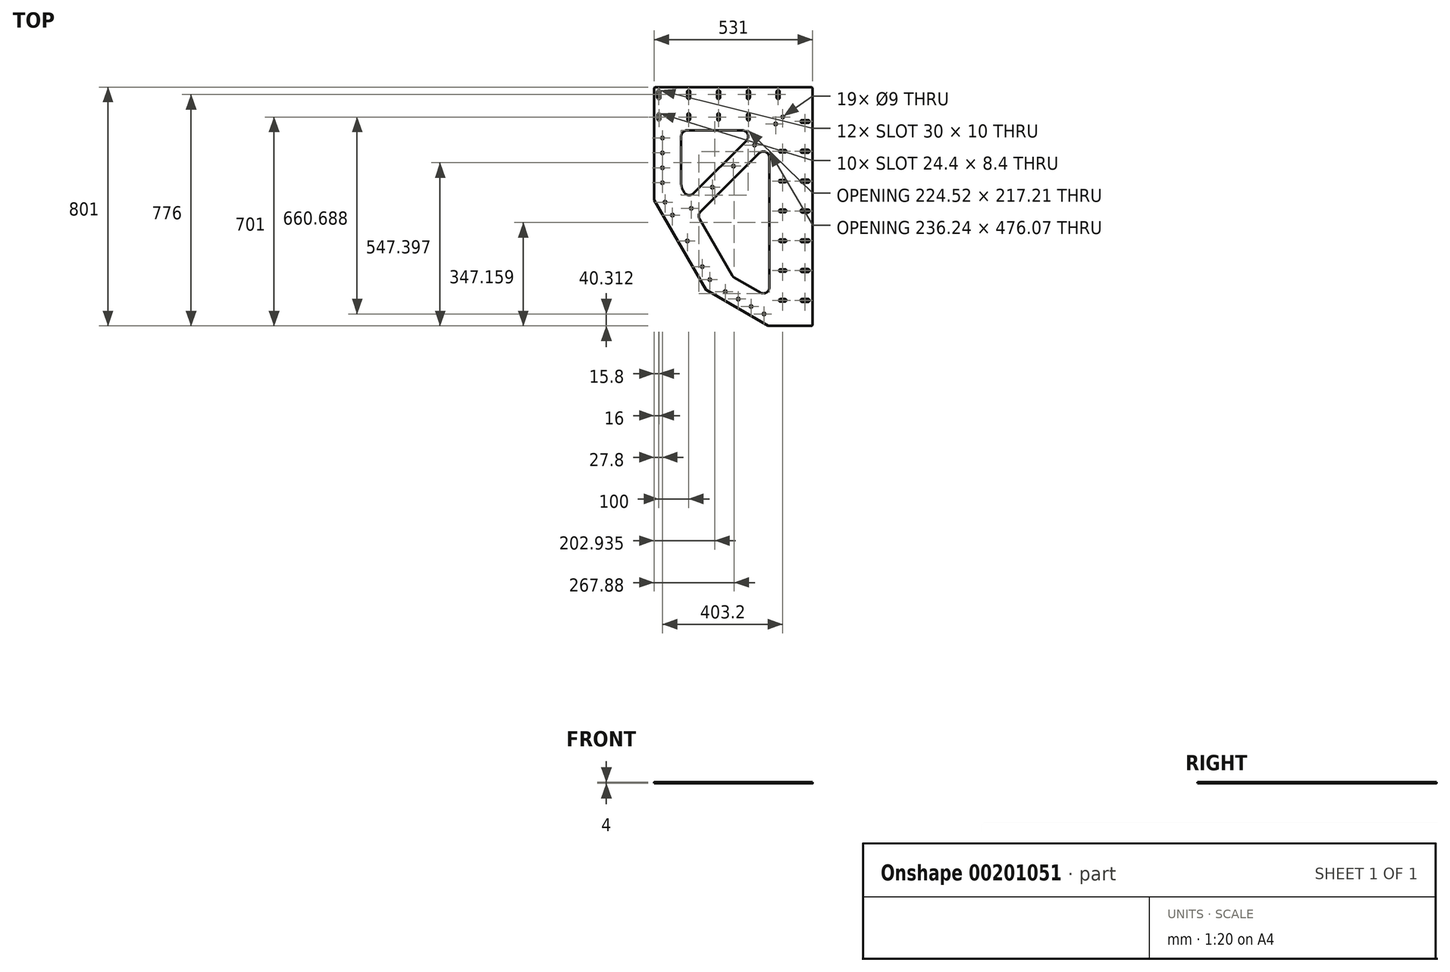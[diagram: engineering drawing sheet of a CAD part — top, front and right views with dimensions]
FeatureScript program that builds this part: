
annotation { "Feature Type Name" : "Feature", "Feature Type Description" : "" }
export const myFeature = defineFeature(function(context is Context, id is Id, definition is map)
    precondition{}
    {
        {
            var Q0;
            Q0=qCreatedBy(makeId("Top.planeOp"),FACE);
            var sketch = newSketch(context, id + "F0", { "sketchPlane" : qUnion([Q0])});
            skLineSegment(sketch, "E0.bottom", {"start": v(750, -750) * mm, "end": v(-750, -750) * mm});
            skLineSegment(sketch, "E0.top", {"start": v(750, 750) * mm, "end": v(-750, 750) * mm});
            skLineSegment(sketch, "E0.left", {"start": v(750, -750) * mm, "end": v(750, 750) * mm});
            skLineSegment(sketch, "E0.right", {"start": v(-750, -750) * mm, "end": v(-750, 750) * mm});
            skPoint(sketch, "E0.middle", {"position": v(0, 0) * mm});
            skSolve(sketch);
        }
        {
            var Q0;
            Q0=qSketchRegion(id+"F0",true);
            extrude(context, id + "F1", {"entities" : qUnion([Q0]), "depth" : 4 * mm});
        }
        {
            var Q0;
            Q0=makeQuery(id+"F1.opExtrude","CAP_FACE",FACE,{"disambiguationData":[OSD([sQuery(id+"F0.wireOp",EDGE,"E0.bottom"),sQuery(id+"F0.wireOp",EDGE,"E0.top"),sQuery(id+"F0.wireOp",EDGE,"E0.left"),sQuery(id+"F0.wireOp",EDGE,"E0.right")])],"isStart":false});
            var sketch = newSketch(context, id + "F2", { "sketchPlane" : qUnion([Q0])});
            skLineSegment(sketch, "E1", {"start": v(0, -750) * mm, "end": v(0, 750) * mm, "construction": true});
            skCircle(sketch, "E2", {"center": v(0, 71) * mm, "radius": 559 * mm, "construction": true});
            skCircle(sketch, "E3", {"center": v(0, 630) * mm, "radius": 7.5 * mm});
            skLineSegment(sketch, "E4", {"start": v(0, 71) * mm, "end": v(-275.24, -87.91) * mm, "construction": true});
            skLineSegment(sketch, "E5", {"start": v(0, 71) * mm, "end": v(329.13, -119.03) * mm, "construction": true});
            skCircle(sketch, "E6.MirrorC", {"center": v(-484.1, -208.5) * mm, "radius": 7.5 * mm});
            skCircle(sketch, "E7.MirrorC", {"center": v(484.1, -208.5) * mm, "radius": 7.5 * mm});
            skCircle(sketch, "E8", {"center": v(0, 71) * mm, "radius": 362 * mm, "construction": true});
            skCircle(sketch, "E9", {"center": v(0, 71) * mm, "radius": 409.5 * mm, "construction": true});
            skCircle(sketch, "E10", {"center": v(-92, 470.03) * mm, "radius": 7.5 * mm});
            skCircle(sketch, "E11.MirrorC", {"center": v(92, 470.03) * mm, "radius": 7.5 * mm});
            skCircle(sketch, "E12", {"center": v(-127, 410) * mm, "radius": 7.5 * mm});
            skCircle(sketch, "E13.MirrorC", {"center": v(127, 410) * mm, "radius": 7.5 * mm});
            skCircle(sketch, "E14.MirrorC", {"center": v(-230.07, -208.48) * mm, "radius": 7.5 * mm});
            skCircle(sketch, "E15.MirrorC", {"center": v(-357.07, 11.49) * mm, "radius": 7.5 * mm});
            skCircle(sketch, "E16.MirrorC", {"center": v(-299.57, -208.2) * mm, "radius": 7.5 * mm});
            skCircle(sketch, "E17.MirrorC", {"center": v(-391.57, -48.84) * mm, "radius": 7.5 * mm});
            skCircle(sketch, "E18.MirrorC", {"center": v(391.57, -48.84) * mm, "radius": 7.5 * mm});
            skCircle(sketch, "E19.MirrorC", {"center": v(299.57, -208.2) * mm, "radius": 7.5 * mm});
            skCircle(sketch, "E20.MirrorC", {"center": v(230.07, -208.48) * mm, "radius": 7.5 * mm});
            skCircle(sketch, "E21.MirrorC", {"center": v(357.07, 11.49) * mm, "radius": 7.5 * mm});
            skPoint(sketch, "E22.middle", {"position": v(0, 435.08) * mm});
            skCircle(sketch, "E23", {"center": v(0, 430) * mm, "radius": 7.5 * mm});
            skCircle(sketch, "E24.MirrorC", {"center": v(310.9, -108.5) * mm, "radius": 7.5 * mm});
            skCircle(sketch, "E25.MirrorC", {"center": v(-310.9, -108.5) * mm, "radius": 7.5 * mm});
            skSolve(sketch);
        }
        {
            var Q0;
            Q0=qSketchRegion(id+"F2",true);
            extrude(context, id + "F3", {"entities" : qUnion([Q0]), "operationType" : NewBodyOperationType.REMOVE, "endBound" : BoundingType.THROUGH_ALL, "oppositeDirection" : true, "depth" : 25 * mm});
        }
        {
            var Q0;
            Q0=makeQuery(id+"F1.opExtrude","CAP_FACE",FACE,{"disambiguationData":[OSD([sQuery(id+"F0.wireOp",EDGE,"E0.bottom"),sQuery(id+"F0.wireOp",EDGE,"E0.top"),sQuery(id+"F0.wireOp",EDGE,"E0.left"),sQuery(id+"F0.wireOp",EDGE,"E0.right")])],"isStart":false});
            var sketch = newSketch(context, id + "F4", { "sketchPlane" : qUnion([Q0])});
            skLineSegment(sketch, "E26", {"start": v(0, 750) * mm, "end": v(0, -750) * mm, "construction": true});
            skLineSegment(sketch, "E27", {"start": v(-627.57, 670) * mm, "end": v(-374.68, 670) * mm});
            skLineSegment(sketch, "E28", {"start": v(-397.7, 440.12) * mm, "end": v(-627.57, 670) * mm});
            skLineSegment(sketch, "E29.MirrorCS", {"start": v(627.57, 670) * mm, "end": v(374.68, 670) * mm});
            skLineSegment(sketch, "E30.MirrorCS", {"start": v(397.7, 440.12) * mm, "end": v(627.57, 670) * mm});
            skLineSegment(sketch, "E31", {"start": v(-257.5, 299.93) * mm, "end": v(257.5, 299.93) * mm, "construction": true});
            skLineSegment(sketch, "E32", {"start": v(257.5, 299.93) * mm, "end": v(0, 42.43) * mm});
            skLineSegment(sketch, "E33.MirrorCS", {"start": v(-257.5, 299.93) * mm, "end": v(0, 42.43) * mm});
            skLineSegment(sketch, "E34", {"start": v(-399.35, 0) * mm, "end": v(437.87, 0) * mm, "construction": true});
            skLineSegment(sketch, "E35.MirrorCS", {"start": v(-257.5, -299.93) * mm, "end": v(0, -42.43) * mm});
            skLineSegment(sketch, "E36.MirrorCS", {"start": v(-257.5, -299.93) * mm, "end": v(257.5, -299.93) * mm, "construction": true});
            skLineSegment(sketch, "E37.MirrorCS", {"start": v(257.5, -299.93) * mm, "end": v(0, -42.43) * mm});
            skLineSegment(sketch, "E38", {"start": v(-215.67, -173.24) * mm, "end": v(-42.43, 0) * mm});
            skLineSegment(sketch, "E39.MirrorCS", {"start": v(-215.67, 173.24) * mm, "end": v(-42.43, 0) * mm});
            skLineSegment(sketch, "E40.MirrorCS", {"start": v(215.67, 173.24) * mm, "end": v(42.43, 0) * mm});
            skLineSegment(sketch, "E41.MirrorCS", {"start": v(215.67, -173.24) * mm, "end": v(42.43, 0) * mm});
            skLineSegment(sketch, "E42", {"start": v(750, 750) * mm, "end": v(-750, -750) * mm, "construction": true});
            skLineSegment(sketch, "E43", {"start": v(-750, 750) * mm, "end": v(750, -750) * mm, "construction": true});
            skLineSegment(sketch, "E44", {"start": v(-750, -707.57) * mm, "end": v(707.57, 750) * mm, "construction": true});
            skLineSegment(sketch, "E45", {"start": v(750, 707.57) * mm, "end": v(-707.57, -750) * mm, "construction": true});
            skLineSegment(sketch, "E46", {"start": v(-215.67, 173.24) * mm, "end": v(-315.69, 0) * mm, "construction": true});
            skLineSegment(sketch, "E47", {"start": v(-315.69, 0) * mm, "end": v(-215.67, -173.24) * mm});
            skLineSegment(sketch, "E48.MirrorCS", {"start": v(315.69, 0) * mm, "end": v(215.67, -173.24) * mm});
            skLineSegment(sketch, "E49.MirrorCS", {"start": v(215.67, 173.24) * mm, "end": v(315.69, 0) * mm, "construction": true});
            skLineSegment(sketch, "E50", {"start": v(670, 627.57) * mm, "end": v(428.76, 386.33) * mm});
            skLineSegment(sketch, "E51", {"start": v(670, 108.48) * mm, "end": v(670, 627.57) * mm});
            skLineSegment(sketch, "E52", {"start": v(-184.6, -227.04) * mm, "end": v(-257.5, -299.93) * mm});
            skLineSegment(sketch, "E53", {"start": v(-184.6, -227.04) * mm, "end": v(184.6, -227.04) * mm, "construction": true});
            skLineSegment(sketch, "E54", {"start": v(257.5, -299.93) * mm, "end": v(184.6, -227.04) * mm});
            skLineSegment(sketch, "E55", {"start": v(-670, -227.57) * mm, "end": v(-670, -627.57) * mm});
            skLineSegment(sketch, "E56", {"start": v(-670, -627.57) * mm, "end": v(-523.59, -481.16) * mm});
            skLineSegment(sketch, "E57", {"start": v(-523.59, -481.16) * mm, "end": v(-670, -227.57) * mm});
            skLineSegment(sketch, "E58.MirrorCS", {"start": v(523.59, -481.16) * mm, "end": v(670, -227.57) * mm});
            skLineSegment(sketch, "E59.MirrorCS", {"start": v(670, -627.57) * mm, "end": v(523.59, -481.16) * mm});
            skLineSegment(sketch, "E60.MirrorCS", {"start": v(670, -227.57) * mm, "end": v(670, -627.57) * mm});
            skLineSegment(sketch, "E61", {"start": v(0, -450) * mm, "end": v(-117.15, -450) * mm});
            skLineSegment(sketch, "E62", {"start": v(-117.15, -450) * mm, "end": v(-325, -570) * mm});
            skLineSegment(sketch, "E63", {"start": v(-325, -570) * mm, "end": v(0, -570) * mm, "construction": true});
            skLineSegment(sketch, "E64.MirrorCS", {"start": v(0, -450) * mm, "end": v(117.15, -450) * mm});
            skLineSegment(sketch, "E65.MirrorCS", {"start": v(325, -570) * mm, "end": v(0, -570) * mm, "construction": true});
            skLineSegment(sketch, "E66.MirrorCS", {"start": v(117.15, -450) * mm, "end": v(325, -570) * mm});
            skLineSegment(sketch, "E67.MirrorCS", {"start": v(-670, 108.48) * mm, "end": v(-670, 627.57) * mm});
            skLineSegment(sketch, "E68.MirrorCS", {"start": v(-670, 627.57) * mm, "end": v(-428.76, 386.33) * mm});
            skLineSegment(sketch, "E69", {"start": v(428.76, 386.33) * mm, "end": v(548.76, 178.48) * mm});
            skLineSegment(sketch, "E70", {"start": v(548.76, 178.48) * mm, "end": v(670, 108.48) * mm});
            skLineSegment(sketch, "E71.MirrorCS", {"start": v(-428.76, 386.33) * mm, "end": v(-548.76, 178.48) * mm});
            skLineSegment(sketch, "E72.MirrorCS", {"start": v(-548.76, 178.48) * mm, "end": v(-670, 108.48) * mm});
            skLineSegment(sketch, "E73", {"start": v(-184.6, -227.04) * mm, "end": v(-152.63, -282.43) * mm});
            skLineSegment(sketch, "E74", {"start": v(-152.63, -282.43) * mm, "end": v(0, -282.43) * mm});
            skLineSegment(sketch, "E75.MirrorCS", {"start": v(152.63, -282.43) * mm, "end": v(0, -282.43) * mm});
            skLineSegment(sketch, "E76.MirrorCS", {"start": v(184.6, -227.04) * mm, "end": v(152.63, -282.43) * mm});
            skLineSegment(sketch, "E77", {"start": v(-408.03, 159.94) * mm, "end": v(-88.62, -393.3) * mm, "construction": true});
            skLineSegment(sketch, "E78", {"start": v(-215.67, 173.24) * mm, "end": v(-288.56, 246.13) * mm});
            skLineSegment(sketch, "E79", {"start": v(-288.56, 246.13) * mm, "end": v(-373.18, 99.57) * mm});
            skLineSegment(sketch, "E80", {"start": v(-315.69, 0) * mm, "end": v(-373.18, 99.57) * mm});
            skLineSegment(sketch, "E81.MirrorCS", {"start": v(288.56, 246.13) * mm, "end": v(373.18, 99.57) * mm});
            skLineSegment(sketch, "E82.MirrorCS", {"start": v(315.69, 0) * mm, "end": v(373.18, 99.57) * mm});
            skLineSegment(sketch, "E83.MirrorCS", {"start": v(215.67, 173.24) * mm, "end": v(288.56, 246.13) * mm});
            skLineSegment(sketch, "E84", {"start": v(-257.5, 299.93) * mm, "end": v(-462.8, -55.67) * mm, "construction": true});
            skLineSegment(sketch, "E85", {"start": v(-257.5, 299.93) * mm, "end": v(-211.31, 379.93) * mm});
            skLineSegment(sketch, "E86", {"start": v(-211.31, 379.93) * mm, "end": v(0, 379.93) * mm});
            skLineSegment(sketch, "E87.MirrorCS", {"start": v(211.31, 379.93) * mm, "end": v(0, 379.93) * mm});
            skLineSegment(sketch, "E88.MirrorCS", {"start": v(257.5, 299.93) * mm, "end": v(211.31, 379.93) * mm});
            skLineSegment(sketch, "E89", {"start": v(-325, -570) * mm, "end": v(-267.26, -670) * mm});
            skLineSegment(sketch, "E90", {"start": v(-267.26, -670) * mm, "end": v(0, -670) * mm});
            skLineSegment(sketch, "E91.MirrorCS", {"start": v(267.26, -670) * mm, "end": v(0, -670) * mm});
            skLineSegment(sketch, "E92.MirrorCS", {"start": v(325, -570) * mm, "end": v(267.26, -670) * mm});
            skLineSegment(sketch, "E93", {"start": v(428.76, 386.33) * mm, "end": v(397.7, 440.12) * mm, "construction": true});
            skLineSegment(sketch, "E94", {"start": v(397.7, 440.12) * mm, "end": v(374.68, 480) * mm});
            skLineSegment(sketch, "E95", {"start": v(374.68, 480) * mm, "end": v(374.68, 670) * mm});
            skLineSegment(sketch, "E96.MirrorCS", {"start": v(-374.68, 480) * mm, "end": v(-374.68, 670) * mm});
            skLineSegment(sketch, "E97.MirrorCS", {"start": v(-397.7, 440.12) * mm, "end": v(-374.68, 480) * mm});
            skSolve(sketch);
        }
        {
            var Q0;
            Q0=qSketchRegion(id+"F4",true);
            extrude(context, id + "F5", {"entities" : qUnion([Q0]), "operationType" : NewBodyOperationType.REMOVE, "endBound" : BoundingType.THROUGH_ALL, "oppositeDirection" : true, "depth" : 25 * mm});
        }
        {
            var Q0;
            Q0=makeQuery(id+"F1.opExtrude","CAP_FACE",FACE,{"disambiguationData":[OSD([sQuery(id+"F0.wireOp",EDGE,"E0.bottom"),sQuery(id+"F0.wireOp",EDGE,"E0.top"),sQuery(id+"F0.wireOp",EDGE,"E0.left"),sQuery(id+"F0.wireOp",EDGE,"E0.right")])],"isStart":false});
            var sketch = newSketch(context, id + "F6", { "sketchPlane" : qUnion([Q0])});
            skLineSegment(sketch, "E98", {"start": v(0, 750) * mm, "end": v(0, -750) * mm, "construction": true});
            skLineSegment(sketch, "E99.left", {"start": v(-595.8, 707) * mm, "end": v(-595.8, 723) * mm});
            skLineSegment(sketch, "E99.right", {"start": v(-604.2, 707) * mm, "end": v(-604.2, 723) * mm});
            skPoint(sketch, "E99.middle", {"position": v(-600, 715) * mm});
            skArc(sketch, "E100", {"start": v(-595.8, 723) * mm, "mid": v(-600, 727.2) * mm, "end": v(-604.2, 723) * mm});
            skArc(sketch, "E101", {"start": v(-604.2, 707) * mm, "mid": v(-600, 702.8) * mm, "end": v(-595.8, 707) * mm});
            skLineSegment(sketch, "E102", {"start": v(-604.2, 723) * mm, "end": v(-595.8, 723) * mm, "construction": true});
            skArc(sketch, "E103.1.0.0", {"start": v(-504.2, 707) * mm, "mid": v(-500, 702.8) * mm, "end": v(-495.8, 707) * mm});
            skLineSegment(sketch, "E103.1.0.1", {"start": v(-495.8, 707) * mm, "end": v(-495.8, 723) * mm});
            skArc(sketch, "E103.1.0.2", {"start": v(-495.8, 723) * mm, "mid": v(-500, 727.2) * mm, "end": v(-504.2, 723) * mm});
            skLineSegment(sketch, "E103.1.0.3", {"start": v(-504.2, 707) * mm, "end": v(-504.2, 723) * mm});
            skArc(sketch, "E103.2.0.0", {"start": v(-404.2, 707) * mm, "mid": v(-400, 702.8) * mm, "end": v(-395.8, 707) * mm});
            skLineSegment(sketch, "E103.2.0.1", {"start": v(-395.8, 707) * mm, "end": v(-395.8, 723) * mm});
            skArc(sketch, "E103.2.0.2", {"start": v(-395.8, 723) * mm, "mid": v(-400, 727.2) * mm, "end": v(-404.2, 723) * mm});
            skLineSegment(sketch, "E103.2.0.3", {"start": v(-404.2, 707) * mm, "end": v(-404.2, 723) * mm});
            skArc(sketch, "E103.3.0.0", {"start": v(-304.2, 707) * mm, "mid": v(-300, 702.8) * mm, "end": v(-295.8, 707) * mm});
            skLineSegment(sketch, "E103.3.0.1", {"start": v(-295.8, 707) * mm, "end": v(-295.8, 723) * mm});
            skArc(sketch, "E103.3.0.2", {"start": v(-295.8, 723) * mm, "mid": v(-300, 727.2) * mm, "end": v(-304.2, 723) * mm});
            skLineSegment(sketch, "E103.3.0.3", {"start": v(-304.2, 707) * mm, "end": v(-304.2, 723) * mm});
            skArc(sketch, "E103.4.0.0", {"start": v(-204.2, 707) * mm, "mid": v(-200, 702.8) * mm, "end": v(-195.8, 707) * mm});
            skLineSegment(sketch, "E103.4.0.1", {"start": v(-195.8, 707) * mm, "end": v(-195.8, 723) * mm});
            skArc(sketch, "E103.4.0.2", {"start": v(-195.8, 723) * mm, "mid": v(-200, 727.2) * mm, "end": v(-204.2, 723) * mm});
            skLineSegment(sketch, "E103.4.0.3", {"start": v(-204.2, 707) * mm, "end": v(-204.2, 723) * mm});
            skArc(sketch, "E103.5.0.0", {"start": v(-104.2, 707) * mm, "mid": v(-100, 702.8) * mm, "end": v(-95.8, 707) * mm});
            skLineSegment(sketch, "E103.5.0.1", {"start": v(-95.8, 707) * mm, "end": v(-95.8, 723) * mm});
            skArc(sketch, "E103.5.0.2", {"start": v(-95.8, 723) * mm, "mid": v(-100, 727.2) * mm, "end": v(-104.2, 723) * mm});
            skLineSegment(sketch, "E103.5.0.3", {"start": v(-104.2, 707) * mm, "end": v(-104.2, 723) * mm});
            skArc(sketch, "E103.6.0.0", {"start": v(-4.2, 707) * mm, "mid": v(0, 702.8) * mm, "end": v(4.2, 707) * mm});
            skLineSegment(sketch, "E103.6.0.1", {"start": v(4.2, 707) * mm, "end": v(4.2, 723) * mm});
            skArc(sketch, "E103.6.0.2", {"start": v(4.2, 723) * mm, "mid": v(0, 727.2) * mm, "end": v(-4.2, 723) * mm});
            skLineSegment(sketch, "E103.6.0.3", {"start": v(-4.2, 707) * mm, "end": v(-4.2, 723) * mm});
            skArc(sketch, "E103.7.0.0", {"start": v(95.8, 707) * mm, "mid": v(100, 702.8) * mm, "end": v(104.2, 707) * mm});
            skLineSegment(sketch, "E103.7.0.1", {"start": v(104.2, 707) * mm, "end": v(104.2, 723) * mm});
            skArc(sketch, "E103.7.0.2", {"start": v(104.2, 723) * mm, "mid": v(100, 727.2) * mm, "end": v(95.8, 723) * mm});
            skLineSegment(sketch, "E103.7.0.3", {"start": v(95.8, 707) * mm, "end": v(95.8, 723) * mm});
            skArc(sketch, "E103.8.0.0", {"start": v(195.8, 707) * mm, "mid": v(200, 702.8) * mm, "end": v(204.2, 707) * mm});
            skLineSegment(sketch, "E103.8.0.1", {"start": v(204.2, 707) * mm, "end": v(204.2, 723) * mm});
            skArc(sketch, "E103.8.0.2", {"start": v(204.2, 723) * mm, "mid": v(200, 727.2) * mm, "end": v(195.8, 723) * mm});
            skLineSegment(sketch, "E103.8.0.3", {"start": v(195.8, 707) * mm, "end": v(195.8, 723) * mm});
            skArc(sketch, "E103.9.0.0", {"start": v(295.8, 707) * mm, "mid": v(300, 702.8) * mm, "end": v(304.2, 707) * mm});
            skLineSegment(sketch, "E103.9.0.1", {"start": v(304.2, 707) * mm, "end": v(304.2, 723) * mm});
            skArc(sketch, "E103.9.0.2", {"start": v(304.2, 723) * mm, "mid": v(300, 727.2) * mm, "end": v(295.8, 723) * mm});
            skLineSegment(sketch, "E103.9.0.3", {"start": v(295.8, 707) * mm, "end": v(295.8, 723) * mm});
            skArc(sketch, "E103.10.0.0", {"start": v(395.8, 707) * mm, "mid": v(400, 702.8) * mm, "end": v(404.2, 707) * mm});
            skLineSegment(sketch, "E103.10.0.1", {"start": v(404.2, 707) * mm, "end": v(404.2, 723) * mm});
            skArc(sketch, "E103.10.0.2", {"start": v(404.2, 723) * mm, "mid": v(400, 727.2) * mm, "end": v(395.8, 723) * mm});
            skLineSegment(sketch, "E103.10.0.3", {"start": v(395.8, 707) * mm, "end": v(395.8, 723) * mm});
            skArc(sketch, "E103.11.0.0", {"start": v(495.8, 707) * mm, "mid": v(500, 702.8) * mm, "end": v(504.2, 707) * mm});
            skLineSegment(sketch, "E103.11.0.1", {"start": v(504.2, 707) * mm, "end": v(504.2, 723) * mm});
            skArc(sketch, "E103.11.0.2", {"start": v(504.2, 723) * mm, "mid": v(500, 727.2) * mm, "end": v(495.8, 723) * mm});
            skLineSegment(sketch, "E103.11.0.3", {"start": v(495.8, 707) * mm, "end": v(495.8, 723) * mm});
            skArc(sketch, "E103.12.0.0", {"start": v(595.8, 707) * mm, "mid": v(600, 702.8) * mm, "end": v(604.2, 707) * mm});
            skLineSegment(sketch, "E103.12.0.1", {"start": v(604.2, 707) * mm, "end": v(604.2, 723) * mm});
            skArc(sketch, "E103.12.0.2", {"start": v(604.2, 723) * mm, "mid": v(600, 727.2) * mm, "end": v(595.8, 723) * mm});
            skLineSegment(sketch, "E103.12.0.3", {"start": v(595.8, 707) * mm, "end": v(595.8, 723) * mm});
            skLineSegment(sketch, "E103.direction1", {"start": v(-604.2, 707) * mm, "end": v(-504.2, 707) * mm, "construction": true});
            skLineSegment(sketch, "E104", {"start": v(-750, 723) * mm, "end": v(750, 723) * mm, "construction": true});
            skLineSegment(sketch, "E105", {"start": v(-750, 0) * mm, "end": v(750, 0) * mm, "construction": true});
            skArc(sketch, "E106.MirrorCS", {"start": v(-295.8, -723) * mm, "mid": v(-300, -727.2) * mm, "end": v(-304.2, -723) * mm});
            skArc(sketch, "E107.MirrorCS", {"start": v(-495.8, -723) * mm, "mid": v(-500, -727.2) * mm, "end": v(-504.2, -723) * mm});
            skLineSegment(sketch, "E108.MirrorCS", {"start": v(304.2, -707) * mm, "end": v(304.2, -723) * mm});
            skLineSegment(sketch, "E109.MirrorCS", {"start": v(-495.8, -707) * mm, "end": v(-495.8, -723) * mm});
            skArc(sketch, "E110.MirrorCS", {"start": v(-504.2, -707) * mm, "mid": v(-500, -702.8) * mm, "end": v(-495.8, -707) * mm});
            skLineSegment(sketch, "E111.MirrorCS", {"start": v(-604.2, -723) * mm, "end": v(-595.8, -723) * mm, "construction": true});
            skArc(sketch, "E112.MirrorCS", {"start": v(-604.2, -707) * mm, "mid": v(-600, -702.8) * mm, "end": v(-595.8, -707) * mm});
            skArc(sketch, "E113.MirrorCS", {"start": v(-595.8, -723) * mm, "mid": v(-600, -727.2) * mm, "end": v(-604.2, -723) * mm});
            skLineSegment(sketch, "E114.MirrorCS", {"start": v(-604.2, -707) * mm, "end": v(-604.2, -723) * mm});
            skLineSegment(sketch, "E115.MirrorCS", {"start": v(-295.8, -707) * mm, "end": v(-295.8, -723) * mm});
            skLineSegment(sketch, "E116.MirrorCS", {"start": v(-595.8, -707) * mm, "end": v(-595.8, -723) * mm});
            skArc(sketch, "E117.MirrorCS", {"start": v(-304.2, -707) * mm, "mid": v(-300, -702.8) * mm, "end": v(-295.8, -707) * mm});
            skLineSegment(sketch, "E118.MirrorCS", {"start": v(-304.2, -707) * mm, "end": v(-304.2, -723) * mm});
            skArc(sketch, "E119.MirrorCS", {"start": v(295.8, -707) * mm, "mid": v(300, -702.8) * mm, "end": v(304.2, -707) * mm});
            skArc(sketch, "E120.MirrorCS", {"start": v(304.2, -723) * mm, "mid": v(300, -727.2) * mm, "end": v(295.8, -723) * mm});
            skLineSegment(sketch, "E121.MirrorCS", {"start": v(295.8, -707) * mm, "end": v(295.8, -723) * mm});
            skLineSegment(sketch, "E122.MirrorCS", {"start": v(-504.2, -707) * mm, "end": v(-504.2, -723) * mm});
            skArc(sketch, "E123.MirrorCS", {"start": v(-4.2, -707) * mm, "mid": v(0, -702.8) * mm, "end": v(4.2, -707) * mm});
            skArc(sketch, "E124.MirrorCS", {"start": v(104.2, -723) * mm, "mid": v(100, -727.2) * mm, "end": v(95.8, -723) * mm});
            skLineSegment(sketch, "E125.MirrorCS", {"start": v(-4.2, -707) * mm, "end": v(-4.2, -723) * mm});
            skArc(sketch, "E126.MirrorCS", {"start": v(4.2, -723) * mm, "mid": v(0, -727.2) * mm, "end": v(-4.2, -723) * mm});
            skLineSegment(sketch, "E127.MirrorCS", {"start": v(4.2, -707) * mm, "end": v(4.2, -723) * mm});
            skArc(sketch, "E128.MirrorCS", {"start": v(-195.8, -723) * mm, "mid": v(-200, -727.2) * mm, "end": v(-204.2, -723) * mm});
            skLineSegment(sketch, "E129.MirrorCS", {"start": v(395.8, -707) * mm, "end": v(395.8, -723) * mm});
            skArc(sketch, "E130.MirrorCS", {"start": v(504.2, -723) * mm, "mid": v(500, -727.2) * mm, "end": v(495.8, -723) * mm});
            skLineSegment(sketch, "E131.MirrorCS", {"start": v(-395.8, -707) * mm, "end": v(-395.8, -723) * mm});
            skArc(sketch, "E132.MirrorCS", {"start": v(395.8, -707) * mm, "mid": v(400, -702.8) * mm, "end": v(404.2, -707) * mm});
            skArc(sketch, "E133.MirrorCS", {"start": v(604.2, -723) * mm, "mid": v(600, -727.2) * mm, "end": v(595.8, -723) * mm});
            skLineSegment(sketch, "E134.MirrorCS", {"start": v(204.2, -707) * mm, "end": v(204.2, -723) * mm});
            skLineSegment(sketch, "E135.MirrorCS", {"start": v(-195.8, -707) * mm, "end": v(-195.8, -723) * mm});
            skArc(sketch, "E136.MirrorCS", {"start": v(-404.2, -707) * mm, "mid": v(-400, -702.8) * mm, "end": v(-395.8, -707) * mm});
            skLineSegment(sketch, "E137.MirrorCS", {"start": v(-95.8, -707) * mm, "end": v(-95.8, -723) * mm});
            skLineSegment(sketch, "E138.MirrorCS", {"start": v(495.8, -707) * mm, "end": v(495.8, -723) * mm});
            skLineSegment(sketch, "E139.MirrorCS", {"start": v(95.8, -707) * mm, "end": v(95.8, -723) * mm});
            skLineSegment(sketch, "E140.MirrorCS", {"start": v(-404.2, -707) * mm, "end": v(-404.2, -723) * mm});
            skLineSegment(sketch, "E141.MirrorCS", {"start": v(504.2, -707) * mm, "end": v(504.2, -723) * mm});
            skArc(sketch, "E142.MirrorCS", {"start": v(-104.2, -707) * mm, "mid": v(-100, -702.8) * mm, "end": v(-95.8, -707) * mm});
            skLineSegment(sketch, "E143.MirrorCS", {"start": v(104.2, -707) * mm, "end": v(104.2, -723) * mm});
            skArc(sketch, "E144.MirrorCS", {"start": v(-395.8, -723) * mm, "mid": v(-400, -727.2) * mm, "end": v(-404.2, -723) * mm});
            skArc(sketch, "E145.MirrorCS", {"start": v(-95.8, -723) * mm, "mid": v(-100, -727.2) * mm, "end": v(-104.2, -723) * mm});
            skLineSegment(sketch, "E146.MirrorCS", {"start": v(604.2, -707) * mm, "end": v(604.2, -723) * mm});
            skArc(sketch, "E147.MirrorCS", {"start": v(595.8, -707) * mm, "mid": v(600, -702.8) * mm, "end": v(604.2, -707) * mm});
            skLineSegment(sketch, "E148.MirrorCS", {"start": v(-104.2, -707) * mm, "end": v(-104.2, -723) * mm});
            skLineSegment(sketch, "E149.MirrorCS", {"start": v(595.8, -707) * mm, "end": v(595.8, -723) * mm});
            skArc(sketch, "E150.MirrorCS", {"start": v(495.8, -707) * mm, "mid": v(500, -702.8) * mm, "end": v(504.2, -707) * mm});
            skArc(sketch, "E151.MirrorCS", {"start": v(195.8, -707) * mm, "mid": v(200, -702.8) * mm, "end": v(204.2, -707) * mm});
            skArc(sketch, "E152.MirrorCS", {"start": v(95.8, -707) * mm, "mid": v(100, -702.8) * mm, "end": v(104.2, -707) * mm});
            skArc(sketch, "E153.MirrorCS", {"start": v(204.2, -723) * mm, "mid": v(200, -727.2) * mm, "end": v(195.8, -723) * mm});
            skLineSegment(sketch, "E154.MirrorCS", {"start": v(-204.2, -707) * mm, "end": v(-204.2, -723) * mm});
            skLineSegment(sketch, "E155.MirrorCS", {"start": v(195.8, -707) * mm, "end": v(195.8, -723) * mm});
            skArc(sketch, "E156.MirrorCS", {"start": v(404.2, -723) * mm, "mid": v(400, -727.2) * mm, "end": v(395.8, -723) * mm});
            skLineSegment(sketch, "E157.MirrorCS", {"start": v(404.2, -707) * mm, "end": v(404.2, -723) * mm});
            skArc(sketch, "E158.MirrorCS", {"start": v(-204.2, -707) * mm, "mid": v(-200, -702.8) * mm, "end": v(-195.8, -707) * mm});
            skLineSegment(sketch, "E159.MirrorCS", {"start": v(-604.2, -707) * mm, "end": v(-504.2, -707) * mm, "construction": true});
            skPoint(sketch, "E160.MirrorP", {"position": v(-600, -715) * mm});
            skLineSegment(sketch, "E161", {"start": v(-750, 750) * mm, "end": v(750, -750) * mm, "construction": true});
            skLineSegment(sketch, "E162.MirrorCS", {"start": v(-707, 595.8) * mm, "end": v(-723, 595.8) * mm});
            skLineSegment(sketch, "E163.MirrorCS", {"start": v(-707, 604.2) * mm, "end": v(-723, 604.2) * mm});
            skArc(sketch, "E164.MirrorCS", {"start": v(-723, 595.8) * mm, "mid": v(-727.2, 600) * mm, "end": v(-723, 604.2) * mm});
            skArc(sketch, "E165.MirrorCS", {"start": v(-707, 604.2) * mm, "mid": v(-702.8, 600) * mm, "end": v(-707, 595.8) * mm});
            skLineSegment(sketch, "E166.MirrorCS", {"start": v(-723, 604.2) * mm, "end": v(-723, 595.8) * mm, "construction": true});
            skArc(sketch, "E167.MirrorCS", {"start": v(-723, 495.8) * mm, "mid": v(-727.2, 500) * mm, "end": v(-723, 504.2) * mm});
            skArc(sketch, "E168.MirrorCS", {"start": v(-723, -104.2) * mm, "mid": v(-727.2, -100) * mm, "end": v(-723, -95.8) * mm});
            skLineSegment(sketch, "E169.MirrorCS", {"start": v(-707, 504.2) * mm, "end": v(-723, 504.2) * mm});
            skArc(sketch, "E170.MirrorCS", {"start": v(-723, 295.8) * mm, "mid": v(-727.2, 300) * mm, "end": v(-723, 304.2) * mm});
            skArc(sketch, "E171.MirrorCS", {"start": v(-707, 404.2) * mm, "mid": v(-702.8, 400) * mm, "end": v(-707, 395.8) * mm});
            skArc(sketch, "E172.MirrorCS", {"start": v(-723, -504.2) * mm, "mid": v(-727.2, -500) * mm, "end": v(-723, -495.8) * mm});
            skLineSegment(sketch, "E173.MirrorCS", {"start": v(-707, 395.8) * mm, "end": v(-723, 395.8) * mm});
            skArc(sketch, "E174.MirrorCS", {"start": v(-723, 395.8) * mm, "mid": v(-727.2, 400) * mm, "end": v(-723, 404.2) * mm});
            skLineSegment(sketch, "E175.MirrorCS", {"start": v(-707, -95.8) * mm, "end": v(-723, -95.8) * mm});
            skLineSegment(sketch, "E176.MirrorCS", {"start": v(-707, 304.2) * mm, "end": v(-723, 304.2) * mm});
            skLineSegment(sketch, "E177.MirrorCS", {"start": v(-707, -495.8) * mm, "end": v(-723, -495.8) * mm});
            skArc(sketch, "E178.MirrorCS", {"start": v(-707, -595.8) * mm, "mid": v(-702.8, -600) * mm, "end": v(-707, -604.2) * mm});
            skArc(sketch, "E179.MirrorCS", {"start": v(-707, -195.8) * mm, "mid": v(-702.8, -200) * mm, "end": v(-707, -204.2) * mm});
            skArc(sketch, "E180.MirrorCS", {"start": v(-707, 204.2) * mm, "mid": v(-702.8, 200) * mm, "end": v(-707, 195.8) * mm});
            skLineSegment(sketch, "E181.MirrorCS", {"start": v(-707, -204.2) * mm, "end": v(-723, -204.2) * mm});
            skLineSegment(sketch, "E182.MirrorCS", {"start": v(-707, 195.8) * mm, "end": v(-723, 195.8) * mm});
            skLineSegment(sketch, "E183.MirrorCS", {"start": v(-707, -604.2) * mm, "end": v(-723, -604.2) * mm});
            skArc(sketch, "E184.MirrorCS", {"start": v(-723, -204.2) * mm, "mid": v(-727.2, -200) * mm, "end": v(-723, -195.8) * mm});
            skArc(sketch, "E185.MirrorCS", {"start": v(-723, 195.8) * mm, "mid": v(-727.2, 200) * mm, "end": v(-723, 204.2) * mm});
            skArc(sketch, "E186.MirrorCS", {"start": v(-723, -604.2) * mm, "mid": v(-727.2, -600) * mm, "end": v(-723, -595.8) * mm});
            skLineSegment(sketch, "E187.MirrorCS", {"start": v(-707, -195.8) * mm, "end": v(-723, -195.8) * mm});
            skLineSegment(sketch, "E188.MirrorCS", {"start": v(-707, 204.2) * mm, "end": v(-723, 204.2) * mm});
            skLineSegment(sketch, "E189.MirrorCS", {"start": v(-707, -595.8) * mm, "end": v(-723, -595.8) * mm});
            skArc(sketch, "E190.MirrorCS", {"start": v(-707, -295.8) * mm, "mid": v(-702.8, -300) * mm, "end": v(-707, -304.2) * mm});
            skArc(sketch, "E191.MirrorCS", {"start": v(-707, 104.2) * mm, "mid": v(-702.8, 100) * mm, "end": v(-707, 95.8) * mm});
            skLineSegment(sketch, "E192.MirrorCS", {"start": v(-707, -304.2) * mm, "end": v(-723, -304.2) * mm});
            skLineSegment(sketch, "E193.MirrorCS", {"start": v(-707, 95.8) * mm, "end": v(-723, 95.8) * mm});
            skArc(sketch, "E194.MirrorCS", {"start": v(-723, -304.2) * mm, "mid": v(-727.2, -300) * mm, "end": v(-723, -295.8) * mm});
            skArc(sketch, "E195.MirrorCS", {"start": v(-723, 95.8) * mm, "mid": v(-727.2, 100) * mm, "end": v(-723, 104.2) * mm});
            skLineSegment(sketch, "E196.MirrorCS", {"start": v(-707, -295.8) * mm, "end": v(-723, -295.8) * mm});
            skLineSegment(sketch, "E197.MirrorCS", {"start": v(-707, 104.2) * mm, "end": v(-723, 104.2) * mm});
            skArc(sketch, "E198.MirrorCS", {"start": v(-707, -395.8) * mm, "mid": v(-702.8, -400) * mm, "end": v(-707, -404.2) * mm});
            skArc(sketch, "E199.MirrorCS", {"start": v(-707, 4.2) * mm, "mid": v(-702.8, 0) * mm, "end": v(-707, -4.2) * mm});
            skLineSegment(sketch, "E200.MirrorCS", {"start": v(-707, -404.2) * mm, "end": v(-723, -404.2) * mm});
            skLineSegment(sketch, "E201.MirrorCS", {"start": v(-707, -4.2) * mm, "end": v(-723, -4.2) * mm});
            skLineSegment(sketch, "E202.MirrorCS", {"start": v(-707, 4.2) * mm, "end": v(-723, 4.2) * mm});
            skLineSegment(sketch, "E203.MirrorCS", {"start": v(-707, -395.8) * mm, "end": v(-723, -395.8) * mm});
            skArc(sketch, "E204.MirrorCS", {"start": v(-723, -404.2) * mm, "mid": v(-727.2, -400) * mm, "end": v(-723, -395.8) * mm});
            skArc(sketch, "E205.MirrorCS", {"start": v(-723, -4.2) * mm, "mid": v(-727.2, 0) * mm, "end": v(-723, 4.2) * mm});
            skArc(sketch, "E206.MirrorCS", {"start": v(-707, -95.8) * mm, "mid": v(-702.8, -100) * mm, "end": v(-707, -104.2) * mm});
            skArc(sketch, "E207.MirrorCS", {"start": v(-707, -495.8) * mm, "mid": v(-702.8, -500) * mm, "end": v(-707, -504.2) * mm});
            skLineSegment(sketch, "E208.MirrorCS", {"start": v(-707, -104.2) * mm, "end": v(-723, -104.2) * mm});
            skLineSegment(sketch, "E209.MirrorCS", {"start": v(-707, -504.2) * mm, "end": v(-723, -504.2) * mm});
            skLineSegment(sketch, "E210.MirrorCS", {"start": v(-707, 404.2) * mm, "end": v(-723, 404.2) * mm});
            skArc(sketch, "E211.MirrorCS", {"start": v(-707, 304.2) * mm, "mid": v(-702.8, 300) * mm, "end": v(-707, 295.8) * mm});
            skLineSegment(sketch, "E212.MirrorCS", {"start": v(-707, 295.8) * mm, "end": v(-723, 295.8) * mm});
            skArc(sketch, "E213.MirrorCS", {"start": v(-707, 504.2) * mm, "mid": v(-702.8, 500) * mm, "end": v(-707, 495.8) * mm});
            skLineSegment(sketch, "E214.MirrorCS", {"start": v(-707, 495.8) * mm, "end": v(-723, 495.8) * mm});
            skLineSegment(sketch, "E215.MirrorCS", {"start": v(-707, 604.2) * mm, "end": v(-707, 504.2) * mm, "construction": true});
            skPoint(sketch, "E216.MirrorP", {"position": v(-715, 600) * mm});
            skLineSegment(sketch, "E217", {"start": v(750, 750) * mm, "end": v(-750, -750) * mm, "construction": true});
            skArc(sketch, "E218.MirrorCS", {"start": v(723, -304.2) * mm, "mid": v(727.2, -300) * mm, "end": v(723, -295.8) * mm});
            skArc(sketch, "E219.MirrorCS", {"start": v(723, -4.2) * mm, "mid": v(727.2, 0) * mm, "end": v(723, 4.2) * mm});
            skLineSegment(sketch, "E220.MirrorCS", {"start": v(707, -4.2) * mm, "end": v(723, -4.2) * mm});
            skLineSegment(sketch, "E221.MirrorCS", {"start": v(723, 604.2) * mm, "end": v(723, 595.8) * mm, "construction": true});
            skArc(sketch, "E222.MirrorCS", {"start": v(707, 604.2) * mm, "mid": v(702.8, 600) * mm, "end": v(707, 595.8) * mm});
            skLineSegment(sketch, "E223.MirrorCS", {"start": v(707, 595.8) * mm, "end": v(723, 595.8) * mm});
            skArc(sketch, "E224.MirrorCS", {"start": v(723, 595.8) * mm, "mid": v(727.2, 600) * mm, "end": v(723, 604.2) * mm});
            skArc(sketch, "E225.MirrorCS", {"start": v(723, -104.2) * mm, "mid": v(727.2, -100) * mm, "end": v(723, -95.8) * mm});
            skArc(sketch, "E226.MirrorCS", {"start": v(707, 4.2) * mm, "mid": v(702.8, 0) * mm, "end": v(707, -4.2) * mm});
            skLineSegment(sketch, "E227.MirrorCS", {"start": v(707, 604.2) * mm, "end": v(723, 604.2) * mm});
            skLineSegment(sketch, "E228.MirrorCS", {"start": v(707, 4.2) * mm, "end": v(723, 4.2) * mm});
            skLineSegment(sketch, "E229.MirrorCS", {"start": v(707, 95.8) * mm, "end": v(723, 95.8) * mm});
            skLineSegment(sketch, "E230.MirrorCS", {"start": v(707, -204.2) * mm, "end": v(723, -204.2) * mm});
            skLineSegment(sketch, "E231.MirrorCS", {"start": v(707, -295.8) * mm, "end": v(723, -295.8) * mm});
            skLineSegment(sketch, "E232.MirrorCS", {"start": v(707, 304.2) * mm, "end": v(723, 304.2) * mm});
            skArc(sketch, "E233.MirrorCS", {"start": v(723, 95.8) * mm, "mid": v(727.2, 100) * mm, "end": v(723, 104.2) * mm});
            skLineSegment(sketch, "E234.MirrorCS", {"start": v(707, -395.8) * mm, "end": v(723, -395.8) * mm});
            skArc(sketch, "E235.MirrorCS", {"start": v(707, 104.2) * mm, "mid": v(702.8, 100) * mm, "end": v(707, 95.8) * mm});
            skArc(sketch, "E236.MirrorCS", {"start": v(707, 504.2) * mm, "mid": v(702.8, 500) * mm, "end": v(707, 495.8) * mm});
            skArc(sketch, "E237.MirrorCS", {"start": v(707, 204.2) * mm, "mid": v(702.8, 200) * mm, "end": v(707, 195.8) * mm});
            skLineSegment(sketch, "E238.MirrorCS", {"start": v(707, -104.2) * mm, "end": v(723, -104.2) * mm});
            skArc(sketch, "E239.MirrorCS", {"start": v(723, 395.8) * mm, "mid": v(727.2, 400) * mm, "end": v(723, 404.2) * mm});
            skArc(sketch, "E240.MirrorCS", {"start": v(723, 195.8) * mm, "mid": v(727.2, 200) * mm, "end": v(723, 204.2) * mm});
            skLineSegment(sketch, "E241.MirrorCS", {"start": v(707, 104.2) * mm, "end": v(723, 104.2) * mm});
            skArc(sketch, "E242.MirrorCS", {"start": v(707, -395.8) * mm, "mid": v(702.8, -400) * mm, "end": v(707, -404.2) * mm});
            skLineSegment(sketch, "E243.MirrorCS", {"start": v(707, -595.8) * mm, "end": v(723, -595.8) * mm});
            skArc(sketch, "E244.MirrorCS", {"start": v(723, -604.2) * mm, "mid": v(727.2, -600) * mm, "end": v(723, -595.8) * mm});
            skArc(sketch, "E245.MirrorCS", {"start": v(707, 304.2) * mm, "mid": v(702.8, 300) * mm, "end": v(707, 295.8) * mm});
            skArc(sketch, "E246.MirrorCS", {"start": v(723, -204.2) * mm, "mid": v(727.2, -200) * mm, "end": v(723, -195.8) * mm});
            skArc(sketch, "E247.MirrorCS", {"start": v(707, -195.8) * mm, "mid": v(702.8, -200) * mm, "end": v(707, -204.2) * mm});
            skLineSegment(sketch, "E248.MirrorCS", {"start": v(707, 204.2) * mm, "end": v(723, 204.2) * mm});
            skLineSegment(sketch, "E249.MirrorCS", {"start": v(707, -604.2) * mm, "end": v(723, -604.2) * mm});
            skLineSegment(sketch, "E250.MirrorCS", {"start": v(707, 395.8) * mm, "end": v(723, 395.8) * mm});
            skLineSegment(sketch, "E251.MirrorCS", {"start": v(707, -195.8) * mm, "end": v(723, -195.8) * mm});
            skLineSegment(sketch, "E252.MirrorCS", {"start": v(707, 295.8) * mm, "end": v(723, 295.8) * mm});
            skArc(sketch, "E253.MirrorCS", {"start": v(707, 404.2) * mm, "mid": v(702.8, 400) * mm, "end": v(707, 395.8) * mm});
            skLineSegment(sketch, "E254.MirrorCS", {"start": v(707, -304.2) * mm, "end": v(723, -304.2) * mm});
            skArc(sketch, "E255.MirrorCS", {"start": v(707, -95.8) * mm, "mid": v(702.8, -100) * mm, "end": v(707, -104.2) * mm});
            skArc(sketch, "E256.MirrorCS", {"start": v(723, -504.2) * mm, "mid": v(727.2, -500) * mm, "end": v(723, -495.8) * mm});
            skLineSegment(sketch, "E257.MirrorCS", {"start": v(707, 495.8) * mm, "end": v(723, 495.8) * mm});
            skArc(sketch, "E258.MirrorCS", {"start": v(707, -595.8) * mm, "mid": v(702.8, -600) * mm, "end": v(707, -604.2) * mm});
            skLineSegment(sketch, "E259.MirrorCS", {"start": v(707, 195.8) * mm, "end": v(723, 195.8) * mm});
            skLineSegment(sketch, "E260.MirrorCS", {"start": v(707, -95.8) * mm, "end": v(723, -95.8) * mm});
            skArc(sketch, "E261.MirrorCS", {"start": v(723, 495.8) * mm, "mid": v(727.2, 500) * mm, "end": v(723, 504.2) * mm});
            skLineSegment(sketch, "E262.MirrorCS", {"start": v(707, 404.2) * mm, "end": v(723, 404.2) * mm});
            skArc(sketch, "E263.MirrorCS", {"start": v(723, 295.8) * mm, "mid": v(727.2, 300) * mm, "end": v(723, 304.2) * mm});
            skLineSegment(sketch, "E264.MirrorCS", {"start": v(707, -495.8) * mm, "end": v(723, -495.8) * mm});
            skArc(sketch, "E265.MirrorCS", {"start": v(707, -495.8) * mm, "mid": v(702.8, -500) * mm, "end": v(707, -504.2) * mm});
            skLineSegment(sketch, "E266.MirrorCS", {"start": v(707, -404.2) * mm, "end": v(723, -404.2) * mm});
            skLineSegment(sketch, "E267.MirrorCS", {"start": v(707, -504.2) * mm, "end": v(723, -504.2) * mm});
            skArc(sketch, "E268.MirrorCS", {"start": v(723, -404.2) * mm, "mid": v(727.2, -400) * mm, "end": v(723, -395.8) * mm});
            skArc(sketch, "E269.MirrorCS", {"start": v(707, -295.8) * mm, "mid": v(702.8, -300) * mm, "end": v(707, -304.2) * mm});
            skLineSegment(sketch, "E270.MirrorCS", {"start": v(707, 504.2) * mm, "end": v(723, 504.2) * mm});
            skLineSegment(sketch, "E271.MirrorCS", {"start": v(-750, -750) * mm, "end": v(750, 750) * mm, "construction": true});
            skLineSegment(sketch, "E272.MirrorCS", {"start": v(707, 604.2) * mm, "end": v(707, 504.2) * mm, "construction": true});
            skPoint(sketch, "E273.MirrorP", {"position": v(715, 600) * mm});
            skCircle(sketch, "E274", {"center": v(-715, 715) * mm, "radius": 4.5 * mm});
            skCircle(sketch, "E275.MirrorC", {"center": v(715, 715) * mm, "radius": 4.5 * mm});
            skCircle(sketch, "E276.MirrorC", {"center": v(-715, -715) * mm, "radius": 4.5 * mm});
            skCircle(sketch, "E277.MirrorC", {"center": v(715, -715) * mm, "radius": 4.5 * mm});
            skLineSegment(sketch, "E278", {"start": v(-600, 715) * mm, "end": v(-750, 715) * mm, "construction": true});
            skSolve(sketch);
        }
        {
            var Q0;
            Q0=qSketchRegion(id+"F6",true);
            extrude(context, id + "F7", {"entities" : qUnion([Q0]), "operationType" : NewBodyOperationType.REMOVE, "endBound" : BoundingType.THROUGH_ALL, "oppositeDirection" : true, "depth" : 25 * mm});
        }
        {
            var Q0;
            Q0=makeQuery(id+"F1.opExtrude","CAP_FACE",FACE,{"disambiguationData":[OSD([sQuery(id+"F0.wireOp",EDGE,"E0.bottom"),sQuery(id+"F0.wireOp",EDGE,"E0.top"),sQuery(id+"F0.wireOp",EDGE,"E0.left"),sQuery(id+"F0.wireOp",EDGE,"E0.right")])],"isStart":false});
            var sketch = newSketch(context, id + "F8", { "sketchPlane" : qUnion([Q0])});
            skCircle(sketch, "E279", {"center": v(311.8, 644.43) * mm, "radius": 4.5 * mm});
            skCircle(sketch, "E280", {"center": v(311.8, 544.43) * mm, "radius": 4.5 * mm});
            skCircle(sketch, "E281", {"center": v(345.55, 385.97) * mm, "radius": 4.5 * mm});
            skCircle(sketch, "E282", {"center": v(395.55, 299.37) * mm, "radius": 4.5 * mm});
            skLineSegment(sketch, "E283", {"start": v(311.8, 676.93) * mm, "end": v(311.8, 444.43) * mm, "construction": true});
            skLineSegment(sketch, "E284", {"start": v(311.8, 444.43) * mm, "end": v(479.3, 154.31) * mm, "construction": true});
            skLineSegment(sketch, "E285", {"start": v(395.55, 299.37) * mm, "end": v(242.04, 210.74) * mm, "construction": true});
            skCircle(sketch, "E286.MirrorC", {"center": v(445.55, 212.77) * mm, "radius": 4.5 * mm});
            skCircle(sketch, "E287.MirrorC", {"center": v(565.9, 104.31) * mm, "radius": 4.5 * mm});
            skCircle(sketch, "E288.MirrorC", {"center": v(652.5, 54.31) * mm, "radius": 4.5 * mm});
            skCircle(sketch, "E289", {"center": v(311.8, 494.43) * mm, "radius": 4.5 * mm});
            skCircle(sketch, "E290.MirrorC", {"center": v(522.6, 129.31) * mm, "radius": 4.5 * mm});
            skCircle(sketch, "E291", {"center": v(311.8, 594.43) * mm, "radius": 4.5 * mm});
            skCircle(sketch, "E292.MirrorC", {"center": v(609.2, 79.31) * mm, "radius": 4.5 * mm});
            skCircle(sketch, "E293", {"center": v(320.55, 429.27) * mm, "radius": 4.5 * mm});
            skLineSegment(sketch, "E294", {"start": v(0, 750) * mm, "end": v(0, -750) * mm, "construction": true});
            skPoint(sketch, "E295", {"position": v(311.8, 444.43) * mm});
            skLineSegment(sketch, "E296", {"start": v(127, 410) * mm, "end": v(357.07, 11.49) * mm, "construction": true});
            skPoint(sketch, "E297", {"position": v(242.04, 210.74) * mm});
            skLineSegment(sketch, "E298", {"start": v(218, 450.9) * mm, "end": v(438, 69.85) * mm, "construction": true});
            skLineSegment(sketch, "E299", {"start": v(218, 450.9) * mm, "end": v(0, 450.9) * mm, "construction": true});
            skLineSegment(sketch, "E300.MirrorCS", {"start": v(-218, 450.9) * mm, "end": v(0, 450.9) * mm, "construction": true});
            skLineSegment(sketch, "E301.MirrorCS", {"start": v(-218, 450.9) * mm, "end": v(-438, 69.85) * mm, "construction": true});
            skLineSegment(sketch, "E302", {"start": v(-328, 260.37) * mm, "end": v(-83.95, 119.47) * mm, "construction": true});
            skLineSegment(sketch, "E303.MirrorCS", {"start": v(-438, 69.85) * mm, "end": v(-329, -118.95) * mm, "construction": true});
            skLineSegment(sketch, "E304.MirrorCS", {"start": v(-220, -307.74) * mm, "end": v(-329, -118.95) * mm, "construction": true});
            skLineSegment(sketch, "E305", {"start": v(328, 260.37) * mm, "end": v(242.04, 210.74) * mm, "construction": true});
            skLineSegment(sketch, "E306.MirrorCS", {"start": v(438, 69.85) * mm, "end": v(329, -118.95) * mm, "construction": true});
            skLineSegment(sketch, "E307.MirrorCS", {"start": v(220, -307.74) * mm, "end": v(329, -118.95) * mm, "construction": true});
            skLineSegment(sketch, "E308.MirrorCS", {"start": v(220, -307.74) * mm, "end": v(-220, -307.74) * mm, "construction": true});
            skCircle(sketch, "E309.MirrorC", {"center": v(-522.6, 129.31) * mm, "radius": 4.5 * mm});
            skCircle(sketch, "E310.MirrorC", {"center": v(-565.9, 104.31) * mm, "radius": 4.5 * mm});
            skCircle(sketch, "E311.MirrorC", {"center": v(-609.2, 79.31) * mm, "radius": 4.5 * mm});
            skCircle(sketch, "E312.MirrorC", {"center": v(-652.5, 54.31) * mm, "radius": 4.5 * mm});
            skCircle(sketch, "E313.MirrorC", {"center": v(-311.8, 544.43) * mm, "radius": 4.5 * mm});
            skCircle(sketch, "E314.MirrorC", {"center": v(-311.8, 594.43) * mm, "radius": 4.5 * mm});
            skCircle(sketch, "E315.MirrorC", {"center": v(-311.8, 644.43) * mm, "radius": 4.5 * mm});
            skCircle(sketch, "E316.MirrorC", {"center": v(-311.8, 494.43) * mm, "radius": 4.5 * mm});
            skCircle(sketch, "E317.MirrorC", {"center": v(-320.55, 429.27) * mm, "radius": 4.5 * mm});
            skCircle(sketch, "E318.MirrorC", {"center": v(-345.55, 385.97) * mm, "radius": 4.5 * mm});
            skCircle(sketch, "E319.MirrorC", {"center": v(-395.55, 299.37) * mm, "radius": 4.5 * mm});
            skCircle(sketch, "E320.MirrorC", {"center": v(-445.55, 212.77) * mm, "radius": 4.5 * mm});
            skCircle(sketch, "E321.MirrorC", {"center": v(210.8, -410.74) * mm, "radius": 4.5 * mm});
            skCircle(sketch, "E322.MirrorC", {"center": v(297.4, -460.74) * mm, "radius": 4.5 * mm});
            skCircle(sketch, "E323.MirrorC", {"center": v(340.7, -485.74) * mm, "radius": 4.5 * mm});
            skCircle(sketch, "E324.MirrorC", {"center": v(254.1, -435.74) * mm, "radius": 4.5 * mm});
            skCircle(sketch, "E325.MirrorC", {"center": v(100, -385.74) * mm, "radius": 4.5 * mm});
            skLineSegment(sketch, "E326.MirrorCS", {"start": v(-220, -307.74) * mm, "end": v(220, -307.74) * mm, "construction": true});
            skCircle(sketch, "E327.MirrorC", {"center": v(-150, -385.74) * mm, "radius": 4.5 * mm});
            skCircle(sketch, "E328.MirrorC", {"center": v(0, -385.74) * mm, "radius": 4.5 * mm});
            skCircle(sketch, "E329.MirrorC", {"center": v(-297.4, -460.74) * mm, "radius": 4.5 * mm});
            skCircle(sketch, "E330.MirrorC", {"center": v(-340.7, -485.74) * mm, "radius": 4.5 * mm});
            skCircle(sketch, "E331.MirrorC", {"center": v(-210.8, -410.74) * mm, "radius": 4.5 * mm});
            skCircle(sketch, "E332.MirrorC", {"center": v(-254.1, -435.74) * mm, "radius": 4.5 * mm});
            skCircle(sketch, "E333.MirrorC", {"center": v(-100, -385.74) * mm, "radius": 4.5 * mm});
            skCircle(sketch, "E334.MirrorC", {"center": v(470.55, 169.47) * mm, "radius": 4.5 * mm});
            skCircle(sketch, "E335.MirrorC", {"center": v(150, -385.74) * mm, "radius": 4.5 * mm});
            skCircle(sketch, "E336.MirrorC", {"center": v(-470.55, 169.47) * mm, "radius": 4.5 * mm});
            skCircle(sketch, "E337", {"center": v(-650.82, -131.54) * mm, "radius": 4.5 * mm});
            skCircle(sketch, "E338.1.0.0", {"center": v(-600.82, -218.15) * mm, "radius": 4.5 * mm});
            skCircle(sketch, "E338.2.0.0", {"center": v(-550.82, -304.75) * mm, "radius": 4.5 * mm});
            skCircle(sketch, "E338.3.0.0", {"center": v(-500.82, -391.35) * mm, "radius": 4.5 * mm});
            skCircle(sketch, "E338.4.0.0", {"center": v(-450.82, -477.95) * mm, "radius": 4.5 * mm});
            skLineSegment(sketch, "E338.direction1", {"start": v(-650.82, -131.54) * mm, "end": v(-600.82, -218.15) * mm, "construction": true});
            skCircle(sketch, "E339.0.5.0", {"center": v(-400.82, -564.56) * mm, "radius": 4.5 * mm});
            skCircle(sketch, "E339.0.6.0", {"center": v(-350.82, -651.16) * mm, "radius": 4.5 * mm});
            skLineSegment(sketch, "E340", {"start": v(750, 750) * mm, "end": v(-750, -750) * mm, "construction": true});
            skCircle(sketch, "E341", {"center": v(691.42, 691.42) * mm, "radius": 4.5 * mm});
            skCircle(sketch, "E342.1.0.0", {"center": v(620.71, 620.71) * mm, "radius": 4.5 * mm});
            skCircle(sketch, "E342.2.0.0", {"center": v(550, 550) * mm, "radius": 4.5 * mm});
            skCircle(sketch, "E342.3.0.0", {"center": v(479.29, 479.29) * mm, "radius": 4.5 * mm});
            skCircle(sketch, "E342.4.0.0", {"center": v(408.58, 408.58) * mm, "radius": 4.5 * mm});
            skLineSegment(sketch, "E342.direction1", {"start": v(691.42, 691.42) * mm, "end": v(620.71, 620.71) * mm, "construction": true});
            skCircle(sketch, "E343.MirrorC", {"center": v(-408.58, 408.58) * mm, "radius": 4.5 * mm});
            skCircle(sketch, "E344.MirrorC", {"center": v(-550, 550) * mm, "radius": 4.5 * mm});
            skCircle(sketch, "E345.MirrorC", {"center": v(-479.29, 479.29) * mm, "radius": 4.5 * mm});
            skCircle(sketch, "E346.MirrorC", {"center": v(-620.71, 620.71) * mm, "radius": 4.5 * mm});
            skCircle(sketch, "E347.MirrorC", {"center": v(-691.42, 691.42) * mm, "radius": 4.5 * mm});
            skLineSegment(sketch, "E348", {"start": v(-484.1, -208.5) * mm, "end": v(-575.82, -261.45) * mm, "construction": true});
            skLineSegment(sketch, "E349", {"start": v(-600.82, -218.15) * mm, "end": v(-550.82, -304.75) * mm, "construction": true});
            skCircle(sketch, "E350.MirrorC", {"center": v(600.82, -218.15) * mm, "radius": 4.5 * mm});
            skCircle(sketch, "E351.MirrorC", {"center": v(550.82, -304.75) * mm, "radius": 4.5 * mm});
            skCircle(sketch, "E352.MirrorC", {"center": v(650.82, -131.54) * mm, "radius": 4.5 * mm});
            skCircle(sketch, "E353.MirrorC", {"center": v(450.82, -477.95) * mm, "radius": 4.5 * mm});
            skCircle(sketch, "E354.MirrorC", {"center": v(500.82, -391.35) * mm, "radius": 4.5 * mm});
            skCircle(sketch, "E355.MirrorC", {"center": v(400.82, -564.56) * mm, "radius": 4.5 * mm});
            skCircle(sketch, "E356.MirrorC", {"center": v(350.82, -651.16) * mm, "radius": 4.5 * mm});
            skCircle(sketch, "E357", {"center": v(0, 0) * mm, "radius": 4.5 * mm});
            skCircle(sketch, "E358.0.1.0", {"center": v(-70.71, 70.71) * mm, "radius": 4.5 * mm});
            skCircle(sketch, "E358.0.2.0", {"center": v(-141.42, 141.42) * mm, "radius": 4.5 * mm});
            skCircle(sketch, "E358.0.3.0", {"center": v(-212.13, 212.13) * mm, "radius": 4.5 * mm});
            skCircle(sketch, "E358.0.4.0", {"center": v(-282.84, 282.84) * mm, "radius": 4.5 * mm});
            skLineSegment(sketch, "E358.direction1", {"start": v(0, 0) * mm, "end": v(38.96, 38.96) * mm, "construction": true});
            skLineSegment(sketch, "E358.direction2", {"start": v(0, 0) * mm, "end": v(-70.71, 70.71) * mm, "construction": true});
            skCircle(sketch, "E359.1.0.0", {"center": v(70.71, 70.71) * mm, "radius": 4.5 * mm});
            skCircle(sketch, "E359.2.0.0", {"center": v(141.42, 141.42) * mm, "radius": 4.5 * mm});
            skCircle(sketch, "E359.3.0.0", {"center": v(212.13, 212.13) * mm, "radius": 4.5 * mm});
            skCircle(sketch, "E359.4.0.0", {"center": v(282.84, 282.84) * mm, "radius": 4.5 * mm});
            skLineSegment(sketch, "E359.direction1", {"start": v(0, 0) * mm, "end": v(70.71, 70.71) * mm, "construction": true});
            skCircle(sketch, "E360.1.0.0", {"center": v(-70.71, -70.71) * mm, "radius": 4.5 * mm});
            skCircle(sketch, "E360.2.0.0", {"center": v(-141.42, -141.42) * mm, "radius": 4.5 * mm});
            skLineSegment(sketch, "E360.direction1", {"start": v(0, 0) * mm, "end": v(-70.71, -70.71) * mm, "construction": true});
            skCircle(sketch, "E361.1.0.0", {"center": v(70.71, -70.71) * mm, "radius": 4.5 * mm});
            skCircle(sketch, "E361.2.0.0", {"center": v(141.42, -141.42) * mm, "radius": 4.5 * mm});
            skLineSegment(sketch, "E361.direction1", {"start": v(0, 0) * mm, "end": v(70.71, -70.71) * mm, "construction": true});
            skSolve(sketch);
        }
        {
            var Q0;
            Q0=qSketchRegion(id+"F8",true);
            extrude(context, id + "F9", {"entities" : qUnion([Q0]), "operationType" : NewBodyOperationType.REMOVE, "endBound" : BoundingType.THROUGH_ALL, "oppositeDirection" : true, "depth" : 25 * mm});
        }
        {
            var Q0;
            Q0=makeQuery(id+"F5.boolean.opBoolean","COPY",EDGE,{"derivedFrom":makeQuery(id+"F5.opExtrude","SWEPT_EDGE",EDGE,{"disambiguationData":[OSD([sQuery(id+"F4.wireOp",EDGE,"E27"),sQuery(id+"F4.wireOp",EDGE,"E28")])]})});
            var Q1;
            Q1=makeQuery(id+"F5.boolean.opBoolean","COPY",EDGE,{"derivedFrom":makeQuery(id+"F5.opExtrude","SWEPT_EDGE",EDGE,{"disambiguationData":[OSD([sQuery(id+"F4.wireOp",EDGE,"E27"),sQuery(id+"F4.wireOp",EDGE,"E96.MirrorCS")])]})});
            var Q2;
            Q2=makeQuery(id+"F5.boolean.opBoolean","COPY",EDGE,{"derivedFrom":makeQuery(id+"F5.opExtrude","SWEPT_EDGE",EDGE,{"disambiguationData":[OSD([sQuery(id+"F4.wireOp",EDGE,"E28"),sQuery(id+"F4.wireOp",EDGE,"E97.MirrorCS")])]})});
            var Q3;
            Q3=makeQuery(id+"F5.boolean.opBoolean","COPY",EDGE,{"derivedFrom":makeQuery(id+"F5.opExtrude","SWEPT_EDGE",EDGE,{"disambiguationData":[OSD([sQuery(id+"F4.wireOp",EDGE,"E29.MirrorCS"),sQuery(id+"F4.wireOp",EDGE,"E30.MirrorCS")])]})});
            var Q4;
            Q4=makeQuery(id+"F5.boolean.opBoolean","COPY",EDGE,{"derivedFrom":makeQuery(id+"F5.opExtrude","SWEPT_EDGE",EDGE,{"disambiguationData":[OSD([sQuery(id+"F4.wireOp",EDGE,"E29.MirrorCS"),sQuery(id+"F4.wireOp",EDGE,"E95")])]})});
            var Q5;
            Q5=makeQuery(id+"F5.boolean.opBoolean","COPY",EDGE,{"derivedFrom":makeQuery(id+"F5.opExtrude","SWEPT_EDGE",EDGE,{"disambiguationData":[OSD([sQuery(id+"F4.wireOp",EDGE,"E30.MirrorCS"),sQuery(id+"F4.wireOp",EDGE,"E94")])]})});
            var Q6;
            Q6=makeQuery(id+"F5.boolean.opBoolean","COPY",EDGE,{"derivedFrom":makeQuery(id+"F5.opExtrude","SWEPT_EDGE",EDGE,{"disambiguationData":[OSD([sQuery(id+"F4.wireOp",EDGE,"E67.MirrorCS"),sQuery(id+"F4.wireOp",EDGE,"E68.MirrorCS")])]})});
            var Q7;
            Q7=makeQuery(id+"F5.boolean.opBoolean","COPY",EDGE,{"derivedFrom":makeQuery(id+"F5.opExtrude","SWEPT_EDGE",EDGE,{"disambiguationData":[OSD([sQuery(id+"F4.wireOp",EDGE,"E68.MirrorCS"),sQuery(id+"F4.wireOp",EDGE,"E71.MirrorCS")])]})});
            var Q8;
            Q8=makeQuery(id+"F5.boolean.opBoolean","COPY",EDGE,{"derivedFrom":makeQuery(id+"F5.opExtrude","SWEPT_EDGE",EDGE,{"disambiguationData":[OSD([sQuery(id+"F4.wireOp",EDGE,"E71.MirrorCS"),sQuery(id+"F4.wireOp",EDGE,"E72.MirrorCS")])]})});
            var Q9;
            Q9=makeQuery(id+"F5.boolean.opBoolean","COPY",EDGE,{"derivedFrom":makeQuery(id+"F5.opExtrude","SWEPT_EDGE",EDGE,{"disambiguationData":[OSD([sQuery(id+"F4.wireOp",EDGE,"E67.MirrorCS"),sQuery(id+"F4.wireOp",EDGE,"E72.MirrorCS")])]})});
            var Q10;
            Q10=makeQuery(id+"F5.boolean.opBoolean","COPY",EDGE,{"derivedFrom":makeQuery(id+"F5.opExtrude","SWEPT_EDGE",EDGE,{"disambiguationData":[OSD([sQuery(id+"F4.wireOp",EDGE,"E50"),sQuery(id+"F4.wireOp",EDGE,"E51")])]})});
            var Q11;
            Q11=makeQuery(id+"F5.boolean.opBoolean","COPY",EDGE,{"derivedFrom":makeQuery(id+"F5.opExtrude","SWEPT_EDGE",EDGE,{"disambiguationData":[OSD([sQuery(id+"F4.wireOp",EDGE,"E50"),sQuery(id+"F4.wireOp",EDGE,"E69")])]})});
            var Q12;
            Q12=makeQuery(id+"F5.boolean.opBoolean","COPY",EDGE,{"derivedFrom":makeQuery(id+"F5.opExtrude","SWEPT_EDGE",EDGE,{"disambiguationData":[OSD([sQuery(id+"F4.wireOp",EDGE,"E69"),sQuery(id+"F4.wireOp",EDGE,"E70")])]})});
            var Q13;
            Q13=makeQuery(id+"F5.boolean.opBoolean","COPY",EDGE,{"derivedFrom":makeQuery(id+"F5.opExtrude","SWEPT_EDGE",EDGE,{"disambiguationData":[OSD([sQuery(id+"F4.wireOp",EDGE,"E51"),sQuery(id+"F4.wireOp",EDGE,"E70")])]})});
            var Q14;
            Q14=makeQuery(id+"F5.boolean.opBoolean","COPY",EDGE,{"derivedFrom":makeQuery(id+"F5.opExtrude","SWEPT_EDGE",EDGE,{"disambiguationData":[OSD([sQuery(id+"F4.wireOp",EDGE,"E85"),sQuery(id+"F4.wireOp",EDGE,"E86")])]})});
            var Q15;
            Q15=makeQuery(id+"F5.boolean.opBoolean","COPY",EDGE,{"derivedFrom":makeQuery(id+"F5.opExtrude","SWEPT_EDGE",EDGE,{"disambiguationData":[OSD([sQuery(id+"F4.wireOp",EDGE,"E87.MirrorCS"),sQuery(id+"F4.wireOp",EDGE,"E88.MirrorCS")])]})});
            var Q16;
            Q16=makeQuery(id+"F5.boolean.opBoolean","COPY",EDGE,{"derivedFrom":makeQuery(id+"F5.opExtrude","SWEPT_EDGE",EDGE,{"disambiguationData":[OSD([sQuery(id+"F4.wireOp",EDGE,"E32"),sQuery(id+"F4.wireOp",EDGE,"E88.MirrorCS")])]})});
            var Q17;
            Q17=makeQuery(id+"F5.boolean.opBoolean","COPY",EDGE,{"derivedFrom":makeQuery(id+"F5.opExtrude","SWEPT_EDGE",EDGE,{"disambiguationData":[OSD([sQuery(id+"F4.wireOp",EDGE,"E32"),sQuery(id+"F4.wireOp",EDGE,"E33.MirrorCS")])]})});
            var Q18;
            Q18=makeQuery(id+"F5.boolean.opBoolean","COPY",EDGE,{"derivedFrom":makeQuery(id+"F5.opExtrude","SWEPT_EDGE",EDGE,{"disambiguationData":[OSD([sQuery(id+"F4.wireOp",EDGE,"E33.MirrorCS"),sQuery(id+"F4.wireOp",EDGE,"E85")])]})});
            var Q19;
            Q19=makeQuery(id+"F5.boolean.opBoolean","COPY",EDGE,{"derivedFrom":makeQuery(id+"F5.opExtrude","SWEPT_EDGE",EDGE,{"disambiguationData":[OSD([sQuery(id+"F4.wireOp",EDGE,"E78"),sQuery(id+"F4.wireOp",EDGE,"E79")])]})});
            var Q20;
            Q20=makeQuery(id+"F5.boolean.opBoolean","COPY",EDGE,{"derivedFrom":makeQuery(id+"F5.opExtrude","SWEPT_EDGE",EDGE,{"disambiguationData":[OSD([sQuery(id+"F4.wireOp",EDGE,"E79"),sQuery(id+"F4.wireOp",EDGE,"E80")])]})});
            var Q21;
            Q21=makeQuery(id+"F5.boolean.opBoolean","COPY",EDGE,{"derivedFrom":makeQuery(id+"F5.opExtrude","SWEPT_EDGE",EDGE,{"disambiguationData":[OSD([sQuery(id+"F4.wireOp",EDGE,"E38"),sQuery(id+"F4.wireOp",EDGE,"E39.MirrorCS")])]})});
            var Q22;
            Q22=makeQuery(id+"F5.boolean.opBoolean","COPY",EDGE,{"derivedFrom":makeQuery(id+"F5.opExtrude","SWEPT_EDGE",EDGE,{"disambiguationData":[OSD([sQuery(id+"F4.wireOp",EDGE,"E38"),sQuery(id+"F4.wireOp",EDGE,"E47")])]})});
            var Q23;
            Q23=makeQuery(id+"F5.boolean.opBoolean","COPY",EDGE,{"derivedFrom":makeQuery(id+"F5.opExtrude","SWEPT_EDGE",EDGE,{"disambiguationData":[OSD([sQuery(id+"F4.wireOp",EDGE,"E81.MirrorCS"),sQuery(id+"F4.wireOp",EDGE,"E83.MirrorCS")])]})});
            var Q24;
            Q24=makeQuery(id+"F5.boolean.opBoolean","COPY",EDGE,{"derivedFrom":makeQuery(id+"F5.opExtrude","SWEPT_EDGE",EDGE,{"disambiguationData":[OSD([sQuery(id+"F4.wireOp",EDGE,"E81.MirrorCS"),sQuery(id+"F4.wireOp",EDGE,"E82.MirrorCS")])]})});
            var Q25;
            Q25=makeQuery(id+"F5.boolean.opBoolean","COPY",EDGE,{"derivedFrom":makeQuery(id+"F5.opExtrude","SWEPT_EDGE",EDGE,{"disambiguationData":[OSD([sQuery(id+"F4.wireOp",EDGE,"E41.MirrorCS"),sQuery(id+"F4.wireOp",EDGE,"E48.MirrorCS")])]})});
            var Q26;
            Q26=makeQuery(id+"F5.boolean.opBoolean","COPY",EDGE,{"derivedFrom":makeQuery(id+"F5.opExtrude","SWEPT_EDGE",EDGE,{"disambiguationData":[OSD([sQuery(id+"F4.wireOp",EDGE,"E40.MirrorCS"),sQuery(id+"F4.wireOp",EDGE,"E41.MirrorCS")])]})});
            var Q27;
            Q27=makeQuery(id+"F5.boolean.opBoolean","COPY",EDGE,{"derivedFrom":makeQuery(id+"F5.opExtrude","SWEPT_EDGE",EDGE,{"disambiguationData":[OSD([sQuery(id+"F4.wireOp",EDGE,"E35.MirrorCS"),sQuery(id+"F4.wireOp",EDGE,"E37.MirrorCS")])]})});
            var Q28;
            Q28=makeQuery(id+"F5.boolean.opBoolean","COPY",EDGE,{"derivedFrom":makeQuery(id+"F5.opExtrude","SWEPT_EDGE",EDGE,{"disambiguationData":[OSD([sQuery(id+"F4.wireOp",EDGE,"E37.MirrorCS"),sQuery(id+"F4.wireOp",EDGE,"E76.MirrorCS")])]})});
            var Q29;
            Q29=makeQuery(id+"F5.boolean.opBoolean","COPY",EDGE,{"derivedFrom":makeQuery(id+"F5.opExtrude","SWEPT_EDGE",EDGE,{"disambiguationData":[OSD([sQuery(id+"F4.wireOp",EDGE,"E75.MirrorCS"),sQuery(id+"F4.wireOp",EDGE,"E76.MirrorCS")])]})});
            var Q30;
            Q30=makeQuery(id+"F5.boolean.opBoolean","COPY",EDGE,{"derivedFrom":makeQuery(id+"F5.opExtrude","SWEPT_EDGE",EDGE,{"disambiguationData":[OSD([sQuery(id+"F4.wireOp",EDGE,"E73"),sQuery(id+"F4.wireOp",EDGE,"E74")])]})});
            var Q31;
            Q31=makeQuery(id+"F5.boolean.opBoolean","COPY",EDGE,{"derivedFrom":makeQuery(id+"F5.opExtrude","SWEPT_EDGE",EDGE,{"disambiguationData":[OSD([sQuery(id+"F4.wireOp",EDGE,"E35.MirrorCS"),sQuery(id+"F4.wireOp",EDGE,"E73")])]})});
            var Q32;
            Q32=makeQuery(id+"F5.boolean.opBoolean","COPY",EDGE,{"derivedFrom":makeQuery(id+"F5.opExtrude","SWEPT_EDGE",EDGE,{"disambiguationData":[OSD([sQuery(id+"F4.wireOp",EDGE,"E56"),sQuery(id+"F4.wireOp",EDGE,"E57")])]})});
            var Q33;
            Q33=makeQuery(id+"F5.boolean.opBoolean","COPY",EDGE,{"derivedFrom":makeQuery(id+"F5.opExtrude","SWEPT_EDGE",EDGE,{"disambiguationData":[OSD([sQuery(id+"F4.wireOp",EDGE,"E61"),sQuery(id+"F4.wireOp",EDGE,"E62")])]})});
            var Q34;
            Q34=makeQuery(id+"F5.boolean.opBoolean","COPY",EDGE,{"derivedFrom":makeQuery(id+"F5.opExtrude","SWEPT_EDGE",EDGE,{"disambiguationData":[OSD([sQuery(id+"F4.wireOp",EDGE,"E64.MirrorCS"),sQuery(id+"F4.wireOp",EDGE,"E66.MirrorCS")])]})});
            var Q35;
            Q35=makeQuery(id+"F5.boolean.opBoolean","COPY",EDGE,{"derivedFrom":makeQuery(id+"F5.opExtrude","SWEPT_EDGE",EDGE,{"disambiguationData":[OSD([sQuery(id+"F4.wireOp",EDGE,"E66.MirrorCS"),sQuery(id+"F4.wireOp",EDGE,"E92.MirrorCS")])]})});
            var Q36;
            Q36=makeQuery(id+"F5.boolean.opBoolean","COPY",EDGE,{"derivedFrom":makeQuery(id+"F5.opExtrude","SWEPT_EDGE",EDGE,{"disambiguationData":[OSD([sQuery(id+"F4.wireOp",EDGE,"E91.MirrorCS"),sQuery(id+"F4.wireOp",EDGE,"E92.MirrorCS")])]})});
            var Q37;
            Q37=makeQuery(id+"F5.boolean.opBoolean","COPY",EDGE,{"derivedFrom":makeQuery(id+"F5.opExtrude","SWEPT_EDGE",EDGE,{"disambiguationData":[OSD([sQuery(id+"F4.wireOp",EDGE,"E89"),sQuery(id+"F4.wireOp",EDGE,"E90")])]})});
            var Q38;
            Q38=makeQuery(id+"F5.boolean.opBoolean","COPY",EDGE,{"derivedFrom":makeQuery(id+"F5.opExtrude","SWEPT_EDGE",EDGE,{"disambiguationData":[OSD([sQuery(id+"F4.wireOp",EDGE,"E62"),sQuery(id+"F4.wireOp",EDGE,"E89")])]})});
            var Q39;
            Q39=makeQuery(id+"F5.boolean.opBoolean","COPY",EDGE,{"derivedFrom":makeQuery(id+"F5.opExtrude","SWEPT_EDGE",EDGE,{"disambiguationData":[OSD([sQuery(id+"F4.wireOp",EDGE,"E58.MirrorCS"),sQuery(id+"F4.wireOp",EDGE,"E59.MirrorCS")])]})});
            fillet(context, id + "F10", {"entities" : qUnion([Q0, Q1, Q2, Q3, Q4, Q5, Q6, Q7, Q8, Q9, Q10, Q11, Q12, Q13, Q14, Q15, Q16, Q17, Q18, Q19, Q20, Q21, Q22, Q23, Q24, Q25, Q26, Q27, Q28, Q29, Q30, Q31, Q32, Q33, Q34, Q35, Q36, Q37, Q38, Q39]), "radius" : 20 * mm, "tangentPropagation" : true, "allowEdgeOverflow" : false});
        }
        {
            var Q0;
            Q0=makeQuery(id+"F5.boolean.opBoolean","COPY",EDGE,{"derivedFrom":makeQuery(id+"F5.opExtrude","SWEPT_EDGE",EDGE,{"disambiguationData":[OSD([sQuery(id+"F4.wireOp",EDGE,"E55"),sQuery(id+"F4.wireOp",EDGE,"E57")])]})});
            var Q1;
            Q1=makeQuery(id+"F5.boolean.opBoolean","COPY",EDGE,{"derivedFrom":makeQuery(id+"F5.opExtrude","SWEPT_EDGE",EDGE,{"disambiguationData":[OSD([sQuery(id+"F4.wireOp",EDGE,"E55"),sQuery(id+"F4.wireOp",EDGE,"E56")])]})});
            var Q2;
            Q2=makeQuery(id+"F5.boolean.opBoolean","COPY",EDGE,{"derivedFrom":makeQuery(id+"F5.opExtrude","SWEPT_EDGE",EDGE,{"disambiguationData":[OSD([sQuery(id+"F4.wireOp",EDGE,"E58.MirrorCS"),sQuery(id+"F4.wireOp",EDGE,"E60.MirrorCS")])]})});
            var Q3;
            Q3=makeQuery(id+"F5.boolean.opBoolean","COPY",EDGE,{"derivedFrom":makeQuery(id+"F5.opExtrude","SWEPT_EDGE",EDGE,{"disambiguationData":[OSD([sQuery(id+"F4.wireOp",EDGE,"E59.MirrorCS"),sQuery(id+"F4.wireOp",EDGE,"E60.MirrorCS")])]})});
            fillet(context, id + "F11", {"entities" : qUnion([Q0, Q1, Q2, Q3]), "radius" : 10 * mm, "tangentPropagation" : true, "allowEdgeOverflow" : false});
        }
        {
            var Q0;
            Q0=makeQuery(id+"F5.boolean.opBoolean","COPY",EDGE,{"derivedFrom":makeQuery(id+"F5.opExtrude","SWEPT_EDGE",EDGE,{"disambiguationData":[OSD([sQuery(id+"F4.wireOp",EDGE,"E96.MirrorCS"),sQuery(id+"F4.wireOp",EDGE,"E97.MirrorCS")])]})});
            var Q1;
            Q1=makeQuery(id+"F5.boolean.opBoolean","COPY",EDGE,{"derivedFrom":makeQuery(id+"F5.opExtrude","SWEPT_EDGE",EDGE,{"disambiguationData":[OSD([sQuery(id+"F4.wireOp",EDGE,"E94"),sQuery(id+"F4.wireOp",EDGE,"E95")])]})});
            fillet(context, id + "F12", {"entities" : qUnion([Q0, Q1]), "radius" : 50 * mm, "tangentPropagation" : true, "allowEdgeOverflow" : false});
        }
        {
            var Q0;
            Q0=makeQuery(id+"F1.opExtrude","CAP_FACE",FACE,{"disambiguationData":[OSD([sQuery(id+"F0.wireOp",EDGE,"E0.bottom"),sQuery(id+"F0.wireOp",EDGE,"E0.top"),sQuery(id+"F0.wireOp",EDGE,"E0.left"),sQuery(id+"F0.wireOp",EDGE,"E0.right")])],"isStart":false});
            var sketch = newSketch(context, id + "F13", { "sketchPlane" : qUnion([Q0])});
            skLineSegment(sketch, "E362", {"start": v(0, 750) * mm, "end": v(0, 550.88) * mm, "construction": true});
            skLineSegment(sketch, "E363", {"start": v(-79.13, 750) * mm, "end": v(-750, -411.97) * mm, "construction": true});
            skCircle(sketch, "E364", {"center": v(-235, 480.03) * mm, "radius": 4.1 * mm});
            skCircle(sketch, "E365.1.0.0", {"center": v(-285, 393.43) * mm, "radius": 4.1 * mm});
            skCircle(sketch, "E365.2.0.0", {"center": v(-335, 306.83) * mm, "radius": 4.1 * mm});
            skLineSegment(sketch, "E365.direction1", {"start": v(-235, 480.03) * mm, "end": v(-285, 393.43) * mm, "construction": true});
            skCircle(sketch, "E366.MirrorC", {"center": v(335, 306.83) * mm, "radius": 4.1 * mm});
            skCircle(sketch, "E367.MirrorC", {"center": v(285, 393.43) * mm, "radius": 4.1 * mm});
            skCircle(sketch, "E368.MirrorC", {"center": v(235, 480.03) * mm, "radius": 4.1 * mm});
            skCircle(sketch, "E369.0.3.0", {"center": v(-385, 220.22) * mm, "radius": 4.1 * mm});
            skCircle(sketch, "E370.MirrorC", {"center": v(385, 220.22) * mm, "radius": 4.1 * mm});
            skPoint(sketch, "E371", {"position": v(-92, 470.03) * mm});
            skCircle(sketch, "E372.0.4.0", {"center": v(-435, 133.62) * mm, "radius": 4.1 * mm});
            skCircle(sketch, "E373.MirrorC", {"center": v(435, 133.62) * mm, "radius": 4.1 * mm});
            skCircle(sketch, "E374.0.5.0", {"center": v(-485, 47.02) * mm, "radius": 4.1 * mm});
            skCircle(sketch, "E375.MirrorC", {"center": v(485, 47.02) * mm, "radius": 4.1 * mm});
            skSolve(sketch);
        }
        {
            var Q0;
            Q0=qSketchRegion(id+"F13",true);
            extrude(context, id + "F14", {"entities" : qUnion([Q0]), "operationType" : NewBodyOperationType.REMOVE, "endBound" : BoundingType.THROUGH_ALL, "oppositeDirection" : true, "depth" : 25 * mm});
        }
        {
            var Q0;
            Q0=makeQuery(id+"F1.opExtrude","CAP_FACE",FACE,{"disambiguationData":[OSD([sQuery(id+"F0.wireOp",EDGE,"E0.bottom"),sQuery(id+"F0.wireOp",EDGE,"E0.top"),sQuery(id+"F0.wireOp",EDGE,"E0.left"),sQuery(id+"F0.wireOp",EDGE,"E0.right")])],"isStart":false});
            var sketch = newSketch(context, id + "F15", { "sketchPlane" : qUnion([Q0])});
            skLineSegment(sketch, "E376", {"start": v(-750, 750) * mm, "end": v(284, 750) * mm});
            skLineSegment(sketch, "E377", {"start": v(284, 750) * mm, "end": v(284, 437.2) * mm});
            skLineSegment(sketch, "E378", {"start": v(284, 437.2) * mm, "end": v(459, 134.09) * mm});
            skLineSegment(sketch, "E379", {"start": v(459, 134.09) * mm, "end": v(667, 14) * mm});
            skLineSegment(sketch, "E380", {"start": v(667, 14) * mm, "end": v(750, 14) * mm});
            skLineSegment(sketch, "E381", {"start": v(750, 14) * mm, "end": v(750, -750) * mm});
            skLineSegment(sketch, "E382", {"start": v(750, -750) * mm, "end": v(-750, -750) * mm});
            skLineSegment(sketch, "E383", {"start": v(-750, -750) * mm, "end": v(-750, 750) * mm});
            skSolve(sketch);
        }
        {
            var Q0;
            Q0 = qSketchRegion(id + "F15", true);
            extrude(context, id + "F16", {"entities" : qUnion([Q0]), "operationType" : NewBodyOperationType.REMOVE, "endBound" : BoundingType.THROUGH_ALL, "oppositeDirection" : true, "depth" : 25 * mm});
        }
        {
            var Q0;
            Q0=makeQuery(id+"F1.opExtrude","CAP_FACE",FACE,{"disambiguationData":[OSD([sQuery(id+"F0.wireOp",EDGE,"E0.bottom"),sQuery(id+"F0.wireOp",EDGE,"E0.top"),sQuery(id+"F0.wireOp",EDGE,"E0.left"),sQuery(id+"F0.wireOp",EDGE,"E0.right")])],"isStart":false});
            var sketch = newSketch(context, id + "F17", { "sketchPlane" : qUnion([Q0])});
            skLineSegment(sketch, "E384.bottom", {"start": v(284, 750) * mm, "end": v(815, 750) * mm});
            skLineSegment(sketch, "E384.top", {"start": v(284, 815) * mm, "end": v(815, 815) * mm});
            skLineSegment(sketch, "E384.left", {"start": v(284, 750) * mm, "end": v(284, 815) * mm});
            skLineSegment(sketch, "E384.right", {"start": v(815, 750) * mm, "end": v(815, 815) * mm});
            skLineSegment(sketch, "E385.bottom", {"start": v(750, 14) * mm, "end": v(815, 14) * mm});
            skLineSegment(sketch, "E385.top", {"start": v(750, 750) * mm, "end": v(815, 750) * mm});
            skLineSegment(sketch, "E385.left", {"start": v(750, 14) * mm, "end": v(750, 750) * mm});
            skLineSegment(sketch, "E385.right", {"start": v(815, 14) * mm, "end": v(815, 750) * mm});
            skSolve(sketch);
        }
        {
            var Q0;
            Q0 = qSketchRegion(id + "F17", true);
            extrude(context, id + "F18", {"entities" : qUnion([Q0]), "operationType" : NewBodyOperationType.ADD, "oppositeDirection" : true, "depth" : 4 * mm});
        }
        {
            var Q0;
            Q0=makeQuery(id+"F18.opExtrude","SWEPT_EDGE",EDGE,{"disambiguationData":[OSD([sQuery(id+"F17.wireOp",EDGE,"E384.top"),sQuery(id+"F17.wireOp",EDGE,"E384.left")])]});
            var Q1;
            Q1=makeQuery(id+"F18.opExtrude","SWEPT_EDGE",EDGE,{"disambiguationData":[OSD([sQuery(id+"F17.wireOp",EDGE,"E384.top"),sQuery(id+"F17.wireOp",EDGE,"E384.right")])]});
            var Q2;
            Q2=makeQuery(id+"F18.opExtrude","SWEPT_EDGE",EDGE,{"disambiguationData":[OSD([sQuery(id+"F17.wireOp",EDGE,"E385.bottom"),sQuery(id+"F17.wireOp",EDGE,"E385.right")])]});
            var Q3;
            Q3=makeQuery(id+"F16.boolean.opBoolean","COPY",EDGE,{"derivedFrom":makeQuery(id+"F16.opExtrude","SWEPT_EDGE",EDGE,{"disambiguationData":[OSD([sQuery(id+"F15.wireOp",EDGE,"E379"),sQuery(id+"F15.wireOp",EDGE,"E380")])]})});
            var Q4;
            Q4=makeQuery(id+"F16.boolean.opBoolean","COPY",EDGE,{"derivedFrom":makeQuery(id+"F16.opExtrude","SWEPT_EDGE",EDGE,{"disambiguationData":[OSD([sQuery(id+"F15.wireOp",EDGE,"E378"),sQuery(id+"F15.wireOp",EDGE,"E379")])]})});
            var Q5;
            Q5=makeQuery(id+"F16.boolean.opBoolean","COPY",EDGE,{"derivedFrom":makeQuery(id+"F16.opExtrude","SWEPT_EDGE",EDGE,{"disambiguationData":[OSD([sQuery(id+"F15.wireOp",EDGE,"E377"),sQuery(id+"F15.wireOp",EDGE,"E378")])]})});
            fillet(context, id + "F19", {"entities" : qUnion([Q0, Q1, Q2, Q3, Q4, Q5]), "radius" : 5 * mm, "tangentPropagation" : true, "allowEdgeOverflow" : false});
        }
        {
            var Q0;
            Q0=makeQuery(id+"F18.boolean.opBoolean","MERGE",FACE,{"derivedFrom":[makeQuery(id+"F1.opExtrude","CAP_FACE",FACE,{"disambiguationData":[OSD([sQuery(id+"F0.wireOp",EDGE,"E0.bottom"),sQuery(id+"F0.wireOp",EDGE,"E0.top"),sQuery(id+"F0.wireOp",EDGE,"E0.left"),sQuery(id+"F0.wireOp",EDGE,"E0.right")])],"isStart":false}),makeQuery(id+"F18.opExtrude","CAP_FACE",FACE,{"disambiguationData":[OSD([sQuery(id+"F17.wireOp",EDGE,"E384.bottom"),sQuery(id+"F17.wireOp",EDGE,"E384.top"),sQuery(id+"F17.wireOp",EDGE,"E384.left"),sQuery(id+"F17.wireOp",EDGE,"E384.right"),sQuery(id+"F17.wireOp",EDGE,"E385.bottom"),sQuery(id+"F17.wireOp",EDGE,"E385.left"),sQuery(id+"F17.wireOp",EDGE,"E385.right")])],"isStart":true})]});
            var sketch = newSketch(context, id + "F20", { "sketchPlane" : qUnion([Q0])});
            skLineSegment(sketch, "E386.bottom", {"start": v(294.8, 800) * mm, "end": v(304.8, 800) * mm});
            skLineSegment(sketch, "E386.top", {"start": v(294.8, 780) * mm, "end": v(304.8, 780) * mm});
            skLineSegment(sketch, "E386.left", {"start": v(294.8, 800) * mm, "end": v(294.8, 780) * mm});
            skLineSegment(sketch, "E386.right", {"start": v(304.8, 800) * mm, "end": v(304.8, 780) * mm});
            skArc(sketch, "E387", {"start": v(304.8, 800) * mm, "mid": v(299.8, 805) * mm, "end": v(294.8, 800) * mm});
            skArc(sketch, "E388", {"start": v(294.8, 780) * mm, "mid": v(299.8, 775) * mm, "end": v(304.8, 780) * mm});
            skLineSegment(sketch, "E389.1.0.0", {"start": v(404.8, 800) * mm, "end": v(404.8, 780) * mm});
            skLineSegment(sketch, "E389.1.0.1", {"start": v(394.8, 800) * mm, "end": v(394.8, 780) * mm});
            skArc(sketch, "E389.1.0.2", {"start": v(404.8, 800) * mm, "mid": v(399.8, 805) * mm, "end": v(394.8, 800) * mm});
            skArc(sketch, "E389.1.0.3", {"start": v(394.8, 780) * mm, "mid": v(399.8, 775) * mm, "end": v(404.8, 780) * mm});
            skLineSegment(sketch, "E389.2.0.0", {"start": v(504.8, 800) * mm, "end": v(504.8, 780) * mm});
            skLineSegment(sketch, "E389.2.0.1", {"start": v(494.8, 800) * mm, "end": v(494.8, 780) * mm});
            skArc(sketch, "E389.2.0.2", {"start": v(504.8, 800) * mm, "mid": v(499.8, 805) * mm, "end": v(494.8, 800) * mm});
            skArc(sketch, "E389.2.0.3", {"start": v(494.8, 780) * mm, "mid": v(499.8, 775) * mm, "end": v(504.8, 780) * mm});
            skLineSegment(sketch, "E389.3.0.0", {"start": v(604.8, 800) * mm, "end": v(604.8, 780) * mm});
            skLineSegment(sketch, "E389.3.0.1", {"start": v(594.8, 800) * mm, "end": v(594.8, 780) * mm});
            skArc(sketch, "E389.3.0.2", {"start": v(604.8, 800) * mm, "mid": v(599.8, 805) * mm, "end": v(594.8, 800) * mm});
            skArc(sketch, "E389.3.0.3", {"start": v(594.8, 780) * mm, "mid": v(599.8, 775) * mm, "end": v(604.8, 780) * mm});
            skLineSegment(sketch, "E389.4.0.0", {"start": v(704.8, 800) * mm, "end": v(704.8, 780) * mm});
            skLineSegment(sketch, "E389.4.0.1", {"start": v(694.8, 800) * mm, "end": v(694.8, 780) * mm});
            skArc(sketch, "E389.4.0.2", {"start": v(704.8, 800) * mm, "mid": v(699.8, 805) * mm, "end": v(694.8, 800) * mm});
            skArc(sketch, "E389.4.0.3", {"start": v(694.8, 780) * mm, "mid": v(699.8, 775) * mm, "end": v(704.8, 780) * mm});
            skLineSegment(sketch, "E389.direction1", {"start": v(304.8, 780) * mm, "end": v(404.8, 780) * mm, "construction": true});
            skLineSegment(sketch, "E390.bottom", {"start": v(800, 4.8) * mm, "end": v(800, -5.2) * mm});
            skLineSegment(sketch, "E390.top", {"start": v(780, 4.8) * mm, "end": v(780, -5.2) * mm});
            skLineSegment(sketch, "E390.left", {"start": v(800, 4.8) * mm, "end": v(780, 4.8) * mm});
            skLineSegment(sketch, "E390.right", {"start": v(800, -5.2) * mm, "end": v(780, -5.2) * mm});
            skArc(sketch, "E391", {"start": v(800, -5.2) * mm, "mid": v(805, -0.2) * mm, "end": v(800, 4.8) * mm});
            skArc(sketch, "E392", {"start": v(780, 4.8) * mm, "mid": v(775, -0.2) * mm, "end": v(780, -5.2) * mm});
            skLineSegment(sketch, "E393.direction1", {"start": v(780, -5.2) * mm, "end": v(780, 94.8) * mm, "construction": true});
            skLineSegment(sketch, "E394.0.1.0", {"start": v(800, 94.8) * mm, "end": v(780, 94.8) * mm});
            skLineSegment(sketch, "E394.3.1.0", {"start": v(800, 104.8) * mm, "end": v(780, 104.8) * mm});
            skArc(sketch, "E394.6.1.0", {"start": v(800, 94.8) * mm, "mid": v(805, 99.8) * mm, "end": v(800, 104.8) * mm});
            skArc(sketch, "E394.10.1.0", {"start": v(780, 104.8) * mm, "mid": v(775, 99.8) * mm, "end": v(780, 94.8) * mm});
            skLineSegment(sketch, "E394.0.2.0", {"start": v(800, 194.8) * mm, "end": v(780, 194.8) * mm});
            skLineSegment(sketch, "E394.3.2.0", {"start": v(800, 204.8) * mm, "end": v(780, 204.8) * mm});
            skArc(sketch, "E394.6.2.0", {"start": v(800, 194.8) * mm, "mid": v(805, 199.8) * mm, "end": v(800, 204.8) * mm});
            skArc(sketch, "E394.10.2.0", {"start": v(780, 204.8) * mm, "mid": v(775, 199.8) * mm, "end": v(780, 194.8) * mm});
            skLineSegment(sketch, "E394.0.3.0", {"start": v(800, 294.8) * mm, "end": v(780, 294.8) * mm});
            skLineSegment(sketch, "E394.3.3.0", {"start": v(800, 304.8) * mm, "end": v(780, 304.8) * mm});
            skArc(sketch, "E394.6.3.0", {"start": v(800, 294.8) * mm, "mid": v(805, 299.8) * mm, "end": v(800, 304.8) * mm});
            skArc(sketch, "E394.10.3.0", {"start": v(780, 304.8) * mm, "mid": v(775, 299.8) * mm, "end": v(780, 294.8) * mm});
            skLineSegment(sketch, "E394.0.4.0", {"start": v(800, 394.8) * mm, "end": v(780, 394.8) * mm});
            skLineSegment(sketch, "E394.3.4.0", {"start": v(800, 404.8) * mm, "end": v(780, 404.8) * mm});
            skArc(sketch, "E394.6.4.0", {"start": v(800, 394.8) * mm, "mid": v(805, 399.8) * mm, "end": v(800, 404.8) * mm});
            skArc(sketch, "E394.10.4.0", {"start": v(780, 404.8) * mm, "mid": v(775, 399.8) * mm, "end": v(780, 394.8) * mm});
            skLineSegment(sketch, "E395", {"start": v(699.8, 800) * mm, "end": v(699.8, 780) * mm, "construction": true});
            skPoint(sketch, "E396", {"position": v(699.8, 790) * mm});
            skLineSegment(sketch, "E397", {"start": v(780, 399.8) * mm, "end": v(800, 399.8) * mm, "construction": true});
            skPoint(sketch, "E398", {"position": v(790, 399.8) * mm});
            skLineSegment(sketch, "E399.0.5.0", {"start": v(800, 494.8) * mm, "end": v(780, 494.8) * mm});
            skLineSegment(sketch, "E399.3.5.0", {"start": v(800, 504.8) * mm, "end": v(780, 504.8) * mm});
            skArc(sketch, "E399.6.5.0", {"start": v(800, 494.8) * mm, "mid": v(805, 499.8) * mm, "end": v(800, 504.8) * mm});
            skArc(sketch, "E399.10.5.0", {"start": v(780, 504.8) * mm, "mid": v(775, 499.8) * mm, "end": v(780, 494.8) * mm});
            skLineSegment(sketch, "E400.0.6.0", {"start": v(800, 594.8) * mm, "end": v(780, 594.8) * mm});
            skLineSegment(sketch, "E400.3.6.0", {"start": v(800, 604.8) * mm, "end": v(780, 604.8) * mm});
            skArc(sketch, "E400.6.6.0", {"start": v(800, 594.8) * mm, "mid": v(805, 599.8) * mm, "end": v(800, 604.8) * mm});
            skArc(sketch, "E400.10.6.0", {"start": v(780, 604.8) * mm, "mid": v(775, 599.8) * mm, "end": v(780, 594.8) * mm});
            skLineSegment(sketch, "E401.0.7.0", {"start": v(800, 694.8) * mm, "end": v(780, 694.8) * mm});
            skLineSegment(sketch, "E401.3.7.0", {"start": v(800, 704.8) * mm, "end": v(780, 704.8) * mm});
            skArc(sketch, "E401.6.7.0", {"start": v(800, 694.8) * mm, "mid": v(805, 699.8) * mm, "end": v(800, 704.8) * mm});
            skArc(sketch, "E401.10.7.0", {"start": v(780, 704.8) * mm, "mid": v(775, 699.8) * mm, "end": v(780, 694.8) * mm});
            skLineSegment(sketch, "E402", {"start": v(780, 699.8) * mm, "end": v(800, 699.8) * mm, "construction": true});
            skPoint(sketch, "E403", {"position": v(790, 699.8) * mm});
            skSolve(sketch);
        }
        {
            var Q0;
            Q0 = qSketchRegion(id + "F20", true);
            extrude(context, id + "F21", {"entities" : qUnion([Q0]), "operationType" : NewBodyOperationType.REMOVE, "endBound" : BoundingType.THROUGH_ALL, "oppositeDirection" : true, "depth" : 25 * mm});
        }
    });
